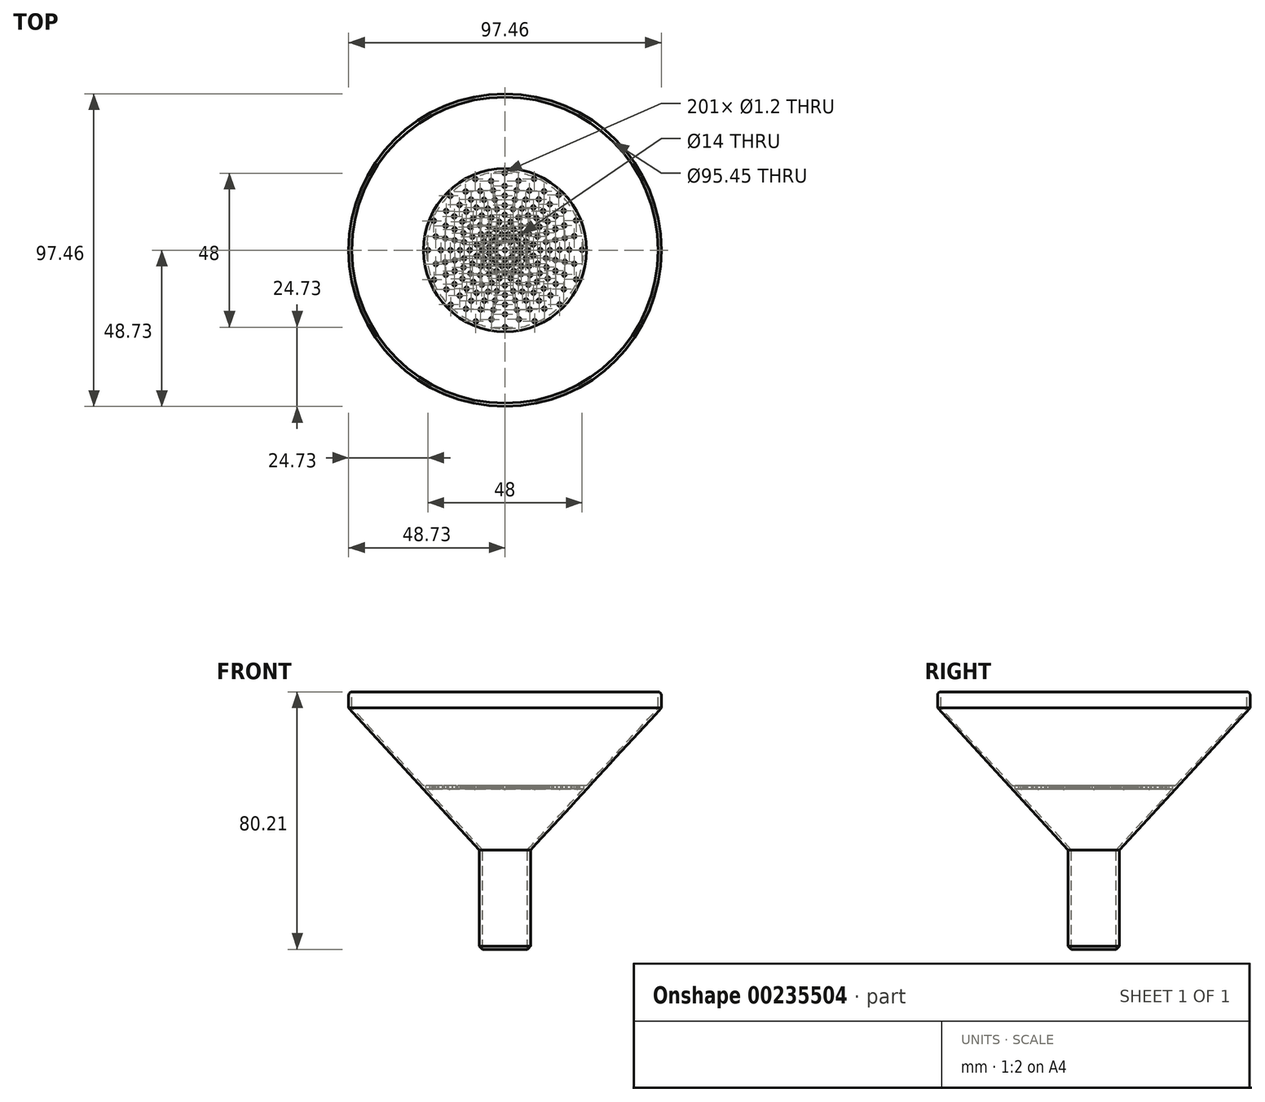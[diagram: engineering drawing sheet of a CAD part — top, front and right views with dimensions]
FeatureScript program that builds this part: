
annotation { "Feature Type Name" : "Feature", "Feature Type Description" : "" }
export const myFeature = defineFeature(function(context is Context, id is Id, definition is map)
    precondition{}
    {
        {
            var Q0;
            Q0=qCreatedBy(makeId("Front.planeOp"),FACE);
            var sketch = newSketch(context, id + "F0", { "sketchPlane" : qUnion([Q0])});
            skLineSegment(sketch, "E0", {"start": v(0, 0) * mm, "end": v(0, -31) * mm, "construction": true});
            skLineSegment(sketch, "E1", {"start": v(0, 0) * mm, "end": v(0, 43) * mm, "construction": true});
            skLineSegment(sketch, "E2", {"start": v(0, -31) * mm, "end": v(8, -31) * mm, "construction": true});
            skLineSegment(sketch, "E3", {"start": v(8, -31) * mm, "end": v(7, -31) * mm});
            skLineSegment(sketch, "E4", {"start": v(7, -31) * mm, "end": v(7, 0) * mm});
            skLineSegment(sketch, "E5", {"start": v(8, -31) * mm, "end": v(8, 0) * mm});
            skLineSegment(sketch, "E6", {"start": v(48.73, 44.2) * mm, "end": v(8, 0) * mm});
            skLineSegment(sketch, "E7", {"start": v(0, 43) * mm, "end": v(0, 41) * mm, "construction": true});
            skLineSegment(sketch, "E8", {"start": v(47.73, 44.2) * mm, "end": v(7, 0) * mm});
            skLineSegment(sketch, "E9", {"start": v(0, 0) * mm, "end": v(0, 20) * mm, "construction": true});
            skLineSegment(sketch, "E10", {"start": v(0, 20) * mm, "end": v(25.42, 20) * mm});
            skLineSegment(sketch, "E11", {"start": v(0, 20) * mm, "end": v(0, 19) * mm, "construction": true});
            skLineSegment(sketch, "E12", {"start": v(0, 19) * mm, "end": v(24.5, 19) * mm});
            skLineSegment(sketch, "E13", {"start": v(47.73, 44.2) * mm, "end": v(47.73, 44.2) * mm});
            skLineSegment(sketch, "E14", {"start": v(47.73, 44.2) * mm, "end": v(48.73, 44.2) * mm});
            skLineSegment(sketch, "E15", {"start": v(0, 19) * mm, "end": v(0, 20) * mm});
            skLineSegment(sketch, "E16", {"start": v(47.73, 44.2) * mm, "end": v(47.73, 49.2) * mm});
            skLineSegment(sketch, "E17", {"start": v(47.73, 49.2) * mm, "end": v(48.73, 49.2) * mm});
            skLineSegment(sketch, "E18", {"start": v(48.73, 49.2) * mm, "end": v(48.73, 44.2) * mm});
            skSolve(sketch);
        }
        {
            var Q0;
            Q0 = qSketchRegion(id + "F0", true);
            var Q1;
            Q1=sQuery(id+"F0.wireOp",EDGE,"E0");
            revolve(context, id + "F1", {"entities" : qUnion([Q0]), "axis" : qUnion([Q1]), "revolveType" : RevolveType.FULL});
        }
        {
            var Q0;
            Q0=makeQuery(id+"F1.opRevolve","SWEPT_EDGE",EDGE,{"disambiguationData":[OSD([sQuery(id+"F0.wireOp",EDGE,"E3"),sQuery(id+"F0.wireOp",EDGE,"E5")])]});
            chamfer(context, id + "F2", {"entities" : qUnion([Q0]), "width" : 1 * mm, "tangentPropagation" : true});
        }
        {
            var Q0;
            Q0=makeQuery(id+"F1.opRevolve","SWEPT_FACE",FACE,{"disambiguationData":[OSD([sQuery(id+"F0.wireOp",EDGE,"E10")])]});
            var sketch = newSketch(context, id + "F3", { "sketchPlane" : qUnion([Q0])});
            skCircle(sketch, "E19", {"center": v(0, 0) * mm, "radius": 0.5 * mm});
            skCircle(sketch, "E20", {"center": v(0, 0) * mm, "radius": 0.5 * mm, "construction": true});
            skCircle(sketch, "E21", {"center": v(0, 0) * mm, "radius": 24 * mm});
            skCircle(sketch, "E22", {"center": v(0, 0) * mm, "radius": 23 * mm});
            skCircle(sketch, "E23", {"center": v(0, 0) * mm, "radius": 22 * mm});
            skCircle(sketch, "E24", {"center": v(0, 0) * mm, "radius": 21 * mm});
            skCircle(sketch, "E25", {"center": v(0, 0) * mm, "radius": 20 * mm});
            skCircle(sketch, "E26", {"center": v(0, 0) * mm, "radius": 19 * mm});
            skCircle(sketch, "E27", {"center": v(0, 0) * mm, "radius": 18 * mm});
            skCircle(sketch, "E28", {"center": v(0, 0) * mm, "radius": 17 * mm});
            skCircle(sketch, "E29", {"center": v(0, 0) * mm, "radius": 16 * mm});
            skCircle(sketch, "E30", {"center": v(0, 0) * mm, "radius": 15 * mm});
            skCircle(sketch, "E31", {"center": v(0, 0) * mm, "radius": 14 * mm});
            skCircle(sketch, "E32", {"center": v(0, 0) * mm, "radius": 13 * mm});
            skCircle(sketch, "E33", {"center": v(0, 0) * mm, "radius": 12 * mm});
            skCircle(sketch, "E34", {"center": v(0, 0) * mm, "radius": 11 * mm});
            skCircle(sketch, "E35", {"center": v(0, 0) * mm, "radius": 10 * mm});
            skCircle(sketch, "E36", {"center": v(0, 0) * mm, "radius": 9 * mm});
            skCircle(sketch, "E37", {"center": v(0, 0) * mm, "radius": 8 * mm});
            skCircle(sketch, "E38", {"center": v(0, 0) * mm, "radius": 7 * mm});
            skCircle(sketch, "E39", {"center": v(0, 0) * mm, "radius": 6 * mm});
            skCircle(sketch, "E40", {"center": v(0, 0) * mm, "radius": 5 * mm});
            skCircle(sketch, "E41", {"center": v(0, 0) * mm, "radius": 4 * mm});
            skCircle(sketch, "E42", {"center": v(0, 0) * mm, "radius": 3 * mm});
            skCircle(sketch, "E43", {"center": v(0, 0) * mm, "radius": 2 * mm});
            skPoint(sketch, "E44", {"position": v(-2, 0) * mm});
            skPoint(sketch, "E45", {"position": v(-5, 0) * mm});
            skPoint(sketch, "E46", {"position": v(-6, 0) * mm});
            skPoint(sketch, "E47", {"position": v(-7, 0) * mm});
            skPoint(sketch, "E48", {"position": v(-8, 0) * mm});
            skPoint(sketch, "E49", {"position": v(-9, 0) * mm});
            skPoint(sketch, "E50", {"position": v(-10, 0) * mm});
            skPoint(sketch, "E51", {"position": v(-11, 0) * mm});
            skPoint(sketch, "E52", {"position": v(-12, 0) * mm});
            skPoint(sketch, "E53", {"position": v(-13, 0) * mm});
            skPoint(sketch, "E54", {"position": v(-14, 0) * mm});
            skPoint(sketch, "E55", {"position": v(-15, 0) * mm});
            skPoint(sketch, "E56", {"position": v(-16, 0) * mm});
            skPoint(sketch, "E57", {"position": v(-17, 0) * mm});
            skPoint(sketch, "E58", {"position": v(-18, 0) * mm});
            skPoint(sketch, "E59", {"position": v(-19, 0) * mm});
            skPoint(sketch, "E60", {"position": v(-20, 0) * mm});
            skPoint(sketch, "E61", {"position": v(-21, 0) * mm});
            skPoint(sketch, "E62", {"position": v(-22, 0) * mm});
            skPoint(sketch, "E63", {"position": v(-23, 0) * mm});
            skPoint(sketch, "E64", {"position": v(-24, 0) * mm});
            skPoint(sketch, "E65", {"position": v(4, 0) * mm});
            skPoint(sketch, "E66", {"position": v(5, 0) * mm});
            skPoint(sketch, "E67", {"position": v(6, 0) * mm});
            skPoint(sketch, "E68", {"position": v(7, 0) * mm});
            skPoint(sketch, "E69", {"position": v(8, 0) * mm});
            skPoint(sketch, "E70", {"position": v(9, 0) * mm});
            skPoint(sketch, "E71", {"position": v(10, 0) * mm});
            skPoint(sketch, "E72", {"position": v(11, 0) * mm});
            skPoint(sketch, "E73", {"position": v(12, 0) * mm});
            skPoint(sketch, "E74", {"position": v(13, 0) * mm});
            skPoint(sketch, "E75", {"position": v(14, 0) * mm});
            skPoint(sketch, "E76", {"position": v(15, 0) * mm});
            skPoint(sketch, "E77", {"position": v(16, 0.11) * mm});
            skPoint(sketch, "E78", {"position": v(17, 0.11) * mm});
            skPoint(sketch, "E79", {"position": v(18, 0.11) * mm});
            skPoint(sketch, "E80", {"position": v(19, 0.11) * mm});
            skPoint(sketch, "E81", {"position": v(20, 0.11) * mm});
            skPoint(sketch, "E82", {"position": v(21, 0.11) * mm});
            skPoint(sketch, "E83", {"position": v(22, 0.11) * mm});
            skPoint(sketch, "E84", {"position": v(23, 0.11) * mm});
            skPoint(sketch, "E85", {"position": v(24, 0.11) * mm});
            skLineSegment(sketch, "E86", {"start": v(24, 0.11) * mm, "end": v(-24, 0) * mm, "construction": true});
            skLineSegment(sketch, "E87", {"start": v(0, -24) * mm, "end": v(-0.11, 24) * mm});
            skLineSegment(sketch, "E88", {"start": v(0, 0) * mm, "end": v(-17.01, 16.93) * mm, "construction": true});
            skLineSegment(sketch, "E89", {"start": v(-24, 0) * mm, "end": v(24, 0.11) * mm, "construction": true});
            skLineSegment(sketch, "E90", {"start": v(-17.01, 16.93) * mm, "end": v(17.01, -16.93) * mm});
            skLineSegment(sketch, "E91", {"start": v(0, 0) * mm, "end": v(16.75, 17.19) * mm});
            skLineSegment(sketch, "E92", {"start": v(0, 0) * mm, "end": v(-16.93, -17.01) * mm});
            skLineSegment(sketch, "E93", {"start": v(0, 0) * mm, "end": v(9.1, 22.2) * mm, "construction": true});
            skLineSegment(sketch, "E94", {"start": v(9.1, 22.2) * mm, "end": v(-9.1, -22.2) * mm});
            skLineSegment(sketch, "E95", {"start": v(-24, 0) * mm, "end": v(24, 0.11) * mm});
            skLineSegment(sketch, "E96", {"start": v(0, 0) * mm, "end": v(22.15, 9.24) * mm});
            skLineSegment(sketch, "E97", {"start": v(22.15, 9.24) * mm, "end": v(-22.15, -9.24) * mm});
            skLineSegment(sketch, "E98", {"start": v(-22.2, 9.13) * mm, "end": v(0, 0) * mm});
            skLineSegment(sketch, "E99", {"start": v(0, 0) * mm, "end": v(22.2, -9.13) * mm});
            skLineSegment(sketch, "E100", {"start": v(0, 0) * mm, "end": v(-9.24, 22.15) * mm});
            skLineSegment(sketch, "E101", {"start": v(0, 0) * mm, "end": v(9.24, -22.15) * mm});
            skPoint(sketch, "E102", {"position": v(-3.7, -1.54) * mm});
            skPoint(sketch, "E103", {"position": v(-5.54, -2.3) * mm});
            skPoint(sketch, "E104", {"position": v(-6.46, -2.7) * mm});
            skPoint(sketch, "E105", {"position": v(-7.38, -3.08) * mm});
            skPoint(sketch, "E106", {"position": v(-8.3, -3.46) * mm});
            skPoint(sketch, "E107", {"position": v(-9.23, -3.85) * mm});
            skPoint(sketch, "E108", {"position": v(-10.15, -4.23) * mm});
            skPoint(sketch, "E109", {"position": v(-11.08, -4.62) * mm});
            skPoint(sketch, "E110", {"position": v(-12, -5) * mm});
            skPoint(sketch, "E111", {"position": v(-12.92, -5.39) * mm});
            skPoint(sketch, "E112", {"position": v(-13.84, -5.77) * mm});
            skPoint(sketch, "E113", {"position": v(-14.77, -6.16) * mm});
            skPoint(sketch, "E114", {"position": v(-15.7, -6.54) * mm});
            skPoint(sketch, "E115", {"position": v(-16.61, -6.93) * mm});
            skPoint(sketch, "E116", {"position": v(-17.54, -7.31) * mm});
            skPoint(sketch, "E117", {"position": v(-18.46, -7.7) * mm});
            skPoint(sketch, "E118", {"position": v(-19.38, -8.08) * mm});
            skPoint(sketch, "E119", {"position": v(-20.3, -8.47) * mm});
            skPoint(sketch, "E120", {"position": v(-21.23, -8.85) * mm});
            skPoint(sketch, "E121", {"position": v(-22.15, -9.24) * mm});
            skPoint(sketch, "E122", {"position": v(-1.41, -1.42) * mm});
            skPoint(sketch, "E123", {"position": v(-2.12, -2.13) * mm});
            skPoint(sketch, "E124", {"position": v(-2.82, -2.84) * mm});
            skPoint(sketch, "E125", {"position": v(-3.53, -3.54) * mm});
            skPoint(sketch, "E126", {"position": v(-4.23, -4.25) * mm});
            skPoint(sketch, "E127", {"position": v(-4.94, -4.96) * mm});
            skPoint(sketch, "E128", {"position": v(-5.64, -5.67) * mm});
            skPoint(sketch, "E129", {"position": v(-6.35, -6.38) * mm});
            skPoint(sketch, "E130", {"position": v(-7.05, -7.09) * mm});
            skPoint(sketch, "E131", {"position": v(-7.76, -7.8) * mm});
            skPoint(sketch, "E132", {"position": v(-8.47, -8.5) * mm});
            skPoint(sketch, "E133", {"position": v(-9.17, -9.21) * mm});
            skPoint(sketch, "E134", {"position": v(-9.88, -9.92) * mm});
            skPoint(sketch, "E135", {"position": v(-10.58, -10.63) * mm});
            skPoint(sketch, "E136", {"position": v(-11.29, -11.34) * mm});
            skPoint(sketch, "E137", {"position": v(-12, -12.05) * mm});
            skPoint(sketch, "E138", {"position": v(-12.7, -12.76) * mm});
            skPoint(sketch, "E139", {"position": v(-13.4, -13.47) * mm});
            skPoint(sketch, "E140", {"position": v(-14.1, -14.18) * mm});
            skPoint(sketch, "E141", {"position": v(-14.81, -14.88) * mm});
            skPoint(sketch, "E142", {"position": v(-15.52, -15.6) * mm});
            skPoint(sketch, "E143", {"position": v(-16.22, -16.3) * mm});
            skPoint(sketch, "E144", {"position": v(-16.93, -17.01) * mm});
            skPoint(sketch, "E145", {"position": v(-0.76, -1.85) * mm});
            skPoint(sketch, "E146", {"position": v(-1.14, -2.78) * mm});
            skPoint(sketch, "E147", {"position": v(-1.52, -3.7) * mm});
            skPoint(sketch, "E148", {"position": v(-1.9, -4.63) * mm});
            skPoint(sketch, "E149", {"position": v(-2.27, -5.55) * mm});
            skPoint(sketch, "E150", {"position": v(-2.65, -6.48) * mm});
            skPoint(sketch, "E151", {"position": v(-3.03, -7.4) * mm});
            skPoint(sketch, "E152", {"position": v(-3.41, -8.33) * mm});
            skPoint(sketch, "E153", {"position": v(-3.8, -9.25) * mm});
            skPoint(sketch, "E154", {"position": v(-4.17, -10.18) * mm});
            skPoint(sketch, "E155", {"position": v(-4.55, -11.1) * mm});
            skPoint(sketch, "E156", {"position": v(-4.94, -12.05) * mm});
            skPoint(sketch, "E157", {"position": v(-5.3, -12.96) * mm});
            skPoint(sketch, "E158", {"position": v(-5.69, -13.88) * mm});
            skPoint(sketch, "E159", {"position": v(-6.06, -14.8) * mm});
            skPoint(sketch, "E160", {"position": v(-6.44, -15.73) * mm});
            skPoint(sketch, "E161", {"position": v(-6.82, -16.66) * mm});
            skPoint(sketch, "E162", {"position": v(-7.2, -17.58) * mm});
            skPoint(sketch, "E163", {"position": v(-7.58, -18.5) * mm});
            skPoint(sketch, "E164", {"position": v(-7.96, -19.43) * mm});
            skPoint(sketch, "E165", {"position": v(-8.34, -20.36) * mm});
            skPoint(sketch, "E166", {"position": v(-8.72, -21.28) * mm});
            skPoint(sketch, "E167", {"position": v(-9.1, -22.2) * mm});
            skPoint(sketch, "E168", {"position": v(0, -24) * mm});
            skPoint(sketch, "E169", {"position": v(0, -23) * mm});
            skPoint(sketch, "E170", {"position": v(0, -22) * mm});
            skPoint(sketch, "E171", {"position": v(0, -20.91) * mm});
            skPoint(sketch, "E172", {"position": v(0, -20) * mm});
            skPoint(sketch, "E173", {"position": v(-0.01, -19) * mm});
            skPoint(sketch, "E174", {"position": v(0, -18) * mm});
            skPoint(sketch, "E175", {"position": v(0, -17) * mm});
            skPoint(sketch, "E176", {"position": v(-0.02, -16) * mm});
            skPoint(sketch, "E177", {"position": v(-0.02, -15) * mm});
            skPoint(sketch, "E178", {"position": v(-0.02, -14) * mm});
            skPoint(sketch, "E179", {"position": v(0, -13) * mm});
            skPoint(sketch, "E180", {"position": v(-0.03, -12) * mm});
            skPoint(sketch, "E181", {"position": v(-0.03, -11) * mm});
            skPoint(sketch, "E182", {"position": v(-0.03, -10) * mm});
            skPoint(sketch, "E183", {"position": v(-0.04, -9) * mm});
            skPoint(sketch, "E184", {"position": v(-0.04, -8) * mm});
            skPoint(sketch, "E185", {"position": v(-0.04, -7) * mm});
            skPoint(sketch, "E186", {"position": v(-0.08, -6) * mm});
            skPoint(sketch, "E187", {"position": v(-0.04, -5) * mm});
            skPoint(sketch, "E188", {"position": v(-0.04, -4) * mm});
            skPoint(sketch, "E189", {"position": v(-0.05, -2) * mm});
            skPoint(sketch, "E190", {"position": v(0.77, -1.85) * mm});
            skPoint(sketch, "E191", {"position": v(2.13, -2.12) * mm});
            skPoint(sketch, "E192", {"position": v(2.77, -1.14) * mm});
            skPoint(sketch, "E193", {"position": v(2.77, 1.15) * mm});
            skPoint(sketch, "E194", {"position": v(2.1, 2.15) * mm});
            skPoint(sketch, "E195", {"position": v(1.14, 2.78) * mm});
            skPoint(sketch, "E196", {"position": v(1.15, -2.77) * mm});
            skPoint(sketch, "E197", {"position": v(1.54, -3.7) * mm});
            skPoint(sketch, "E198", {"position": v(1.92, -4.61) * mm});
            skPoint(sketch, "E199", {"position": v(2.3, -5.54) * mm});
            skPoint(sketch, "E200", {"position": v(2.7, -6.46) * mm});
            skPoint(sketch, "E201", {"position": v(3.08, -7.38) * mm});
            skPoint(sketch, "E202", {"position": v(3.46, -8.3) * mm});
            skPoint(sketch, "E203", {"position": v(3.85, -9.23) * mm});
            skPoint(sketch, "E204", {"position": v(4.23, -10.15) * mm});
            skPoint(sketch, "E205", {"position": v(4.62, -11.08) * mm});
            skPoint(sketch, "E206", {"position": v(5, -12) * mm});
            skPoint(sketch, "E207", {"position": v(5.39, -12.92) * mm});
            skPoint(sketch, "E208", {"position": v(5.77, -13.84) * mm});
            skPoint(sketch, "E209", {"position": v(6.16, -14.77) * mm});
            skPoint(sketch, "E210", {"position": v(6.54, -15.7) * mm});
            skPoint(sketch, "E211", {"position": v(6.93, -16.61) * mm});
            skPoint(sketch, "E212", {"position": v(7.31, -17.54) * mm});
            skPoint(sketch, "E213", {"position": v(7.7, -18.46) * mm});
            skPoint(sketch, "E214", {"position": v(8.08, -19.38) * mm});
            skPoint(sketch, "E215", {"position": v(8.47, -20.3) * mm});
            skPoint(sketch, "E216", {"position": v(8.85, -21.23) * mm});
            skPoint(sketch, "E217", {"position": v(9.24, -22.15) * mm});
            skPoint(sketch, "E218", {"position": v(2.84, -2.82) * mm});
            skPoint(sketch, "E219", {"position": v(3.54, -3.53) * mm});
            skPoint(sketch, "E220", {"position": v(4.25, -4.23) * mm});
            skPoint(sketch, "E221", {"position": v(4.96, -4.94) * mm});
            skPoint(sketch, "E222", {"position": v(5.67, -5.64) * mm});
            skPoint(sketch, "E223", {"position": v(6.38, -6.35) * mm});
            skPoint(sketch, "E224", {"position": v(7.09, -7.05) * mm});
            skPoint(sketch, "E225", {"position": v(7.8, -7.76) * mm});
            skPoint(sketch, "E226", {"position": v(8.5, -8.47) * mm});
            skPoint(sketch, "E227", {"position": v(9.21, -9.17) * mm});
            skPoint(sketch, "E228", {"position": v(9.92, -9.88) * mm});
            skPoint(sketch, "E229", {"position": v(10.63, -10.58) * mm});
            skPoint(sketch, "E230", {"position": v(11.34, -11.29) * mm});
            skPoint(sketch, "E231", {"position": v(12.05, -12) * mm});
            skPoint(sketch, "E232", {"position": v(12.76, -12.7) * mm});
            skPoint(sketch, "E233", {"position": v(13.47, -13.4) * mm});
            skPoint(sketch, "E234", {"position": v(14.18, -14.1) * mm});
            skPoint(sketch, "E235", {"position": v(14.88, -14.81) * mm});
            skPoint(sketch, "E236", {"position": v(15.6, -15.52) * mm});
            skPoint(sketch, "E237", {"position": v(16.3, -16.22) * mm});
            skPoint(sketch, "E238", {"position": v(17.01, -16.93) * mm});
            skPoint(sketch, "E239", {"position": v(22.2, -9.13) * mm});
            skPoint(sketch, "E240", {"position": v(22.15, 9.24) * mm});
            skPoint(sketch, "E241", {"position": v(21.27, -8.75) * mm});
            skPoint(sketch, "E242", {"position": v(21.23, 8.85) * mm});
            skPoint(sketch, "E243", {"position": v(20.3, 8.47) * mm});
            skPoint(sketch, "E244", {"position": v(19.38, 8.08) * mm});
            skPoint(sketch, "E245", {"position": v(18.46, 7.7) * mm});
            skPoint(sketch, "E246", {"position": v(17.54, 7.31) * mm});
            skPoint(sketch, "E247", {"position": v(16.61, 6.93) * mm});
            skPoint(sketch, "E248", {"position": v(15.7, 6.54) * mm});
            skPoint(sketch, "E249", {"position": v(14.77, 6.16) * mm});
            skPoint(sketch, "E250", {"position": v(13.84, 5.77) * mm});
            skPoint(sketch, "E251", {"position": v(12.92, 5.39) * mm});
            skPoint(sketch, "E252", {"position": v(12, 5) * mm});
            skPoint(sketch, "E253", {"position": v(11.08, 4.62) * mm});
            skPoint(sketch, "E254", {"position": v(10.15, 4.23) * mm});
            skPoint(sketch, "E255", {"position": v(9.23, 3.85) * mm});
            skPoint(sketch, "E256", {"position": v(8.3, 3.46) * mm});
            skPoint(sketch, "E257", {"position": v(7.38, 3.08) * mm});
            skPoint(sketch, "E258", {"position": v(6.46, 2.7) * mm});
            skPoint(sketch, "E259", {"position": v(5.54, 2.3) * mm});
            skPoint(sketch, "E260", {"position": v(4.61, 1.92) * mm});
            skPoint(sketch, "E261", {"position": v(3.7, 1.54) * mm});
            skPoint(sketch, "E262", {"position": v(3.7, -1.52) * mm});
            skPoint(sketch, "E263", {"position": v(4.62, -1.9) * mm});
            skPoint(sketch, "E264", {"position": v(5.55, -2.28) * mm});
            skPoint(sketch, "E265", {"position": v(6.47, -2.66) * mm});
            skPoint(sketch, "E266", {"position": v(7.4, -3.04) * mm});
            skPoint(sketch, "E267", {"position": v(8.32, -3.42) * mm});
            skPoint(sketch, "E268", {"position": v(9.25, -3.8) * mm});
            skPoint(sketch, "E269", {"position": v(10.17, -4.19) * mm});
            skPoint(sketch, "E270", {"position": v(11.1, -4.57) * mm});
            skPoint(sketch, "E271", {"position": v(12.02, -4.95) * mm});
            skPoint(sketch, "E272", {"position": v(12.95, -5.33) * mm});
            skPoint(sketch, "E273", {"position": v(13.87, -5.7) * mm});
            skPoint(sketch, "E274", {"position": v(14.8, -6.09) * mm});
            skPoint(sketch, "E275", {"position": v(15.72, -6.47) * mm});
            skPoint(sketch, "E276", {"position": v(16.65, -6.85) * mm});
            skPoint(sketch, "E277", {"position": v(17.57, -7.23) * mm});
            skPoint(sketch, "E278", {"position": v(18.5, -7.6) * mm});
            skPoint(sketch, "E279", {"position": v(19.42, -8) * mm});
            skPoint(sketch, "E280", {"position": v(20.35, -8.37) * mm});
            skPoint(sketch, "E281", {"position": v(-2.77, 1.14) * mm});
            skPoint(sketch, "E282", {"position": v(-3.7, 1.52) * mm});
            skPoint(sketch, "E283", {"position": v(-4.62, 1.9) * mm});
            skPoint(sketch, "E284", {"position": v(-5.55, 2.28) * mm});
            skPoint(sketch, "E285", {"position": v(-6.47, 2.66) * mm});
            skPoint(sketch, "E286", {"position": v(-7.4, 3.04) * mm});
            skPoint(sketch, "E287", {"position": v(-8.32, 3.42) * mm});
            skPoint(sketch, "E288", {"position": v(-9.25, 3.8) * mm});
            skPoint(sketch, "E289", {"position": v(-10.17, 4.19) * mm});
            skPoint(sketch, "E290", {"position": v(-11.1, 4.57) * mm});
            skPoint(sketch, "E291", {"position": v(-12.02, 4.95) * mm});
            skPoint(sketch, "E292", {"position": v(-12.95, 5.33) * mm});
            skPoint(sketch, "E293", {"position": v(-13.87, 5.7) * mm});
            skPoint(sketch, "E294", {"position": v(-14.8, 6.09) * mm});
            skPoint(sketch, "E295", {"position": v(-15.72, 6.47) * mm});
            skPoint(sketch, "E296", {"position": v(-16.65, 6.85) * mm});
            skPoint(sketch, "E297", {"position": v(-17.57, 7.23) * mm});
            skPoint(sketch, "E298", {"position": v(-18.5, 7.6) * mm});
            skPoint(sketch, "E299", {"position": v(-19.42, 8) * mm});
            skPoint(sketch, "E300", {"position": v(-20.35, 8.37) * mm});
            skPoint(sketch, "E301", {"position": v(-21.27, 8.75) * mm});
            skPoint(sketch, "E302", {"position": v(-22.2, 9.13) * mm});
            skPoint(sketch, "E303", {"position": v(-1.42, 1.41) * mm});
            skPoint(sketch, "E304", {"position": v(-2.13, 2.12) * mm});
            skPoint(sketch, "E305", {"position": v(-2.84, 2.82) * mm});
            skPoint(sketch, "E306", {"position": v(-3.54, 3.53) * mm});
            skPoint(sketch, "E307", {"position": v(-4.25, 4.23) * mm});
            skPoint(sketch, "E308", {"position": v(-4.96, 4.94) * mm});
            skPoint(sketch, "E309", {"position": v(-5.67, 5.64) * mm});
            skPoint(sketch, "E310", {"position": v(-6.38, 6.35) * mm});
            skPoint(sketch, "E311", {"position": v(-7.09, 7.05) * mm});
            skPoint(sketch, "E312", {"position": v(-7.8, 7.76) * mm});
            skPoint(sketch, "E313", {"position": v(-8.5, 8.47) * mm});
            skPoint(sketch, "E314", {"position": v(-9.18, 9.13) * mm});
            skPoint(sketch, "E315", {"position": v(-9.92, 9.88) * mm});
            skPoint(sketch, "E316", {"position": v(-10.63, 10.58) * mm});
            skPoint(sketch, "E317", {"position": v(-11.34, 11.29) * mm});
            skPoint(sketch, "E318", {"position": v(-12.05, 12) * mm});
            skPoint(sketch, "E319", {"position": v(-12.76, 12.7) * mm});
            skPoint(sketch, "E320", {"position": v(-13.47, 13.4) * mm});
            skPoint(sketch, "E321", {"position": v(-14.18, 14.1) * mm});
            skPoint(sketch, "E322", {"position": v(-14.88, 14.81) * mm});
            skPoint(sketch, "E323", {"position": v(-15.6, 15.52) * mm});
            skPoint(sketch, "E324", {"position": v(-16.3, 16.22) * mm});
            skPoint(sketch, "E325", {"position": v(-17.01, 16.93) * mm});
            skPoint(sketch, "E326", {"position": v(-9.24, 22.15) * mm});
            skPoint(sketch, "E327", {"position": v(-0.11, 24) * mm});
            skPoint(sketch, "E328", {"position": v(9.1, 22.2) * mm});
            skPoint(sketch, "E329", {"position": v(16.75, 17.19) * mm});
            skPoint(sketch, "E330", {"position": v(-1.54, 3.7) * mm});
            skPoint(sketch, "E331", {"position": v(-2.3, 5.54) * mm});
            skPoint(sketch, "E332", {"position": v(-2.7, 6.46) * mm});
            skPoint(sketch, "E333", {"position": v(-3.08, 7.38) * mm});
            skPoint(sketch, "E334", {"position": v(-3.46, 8.3) * mm});
            skPoint(sketch, "E335", {"position": v(-3.85, 9.23) * mm});
            skPoint(sketch, "E336", {"position": v(-4.23, 10.15) * mm});
            skPoint(sketch, "E337", {"position": v(-4.62, 11.08) * mm});
            skPoint(sketch, "E338", {"position": v(-5, 12) * mm});
            skPoint(sketch, "E339", {"position": v(-5.39, 12.92) * mm});
            skPoint(sketch, "E340", {"position": v(-5.77, 13.84) * mm});
            skPoint(sketch, "E341", {"position": v(-6.16, 14.77) * mm});
            skPoint(sketch, "E342", {"position": v(-6.54, 15.7) * mm});
            skPoint(sketch, "E343", {"position": v(-6.93, 16.61) * mm});
            skPoint(sketch, "E344", {"position": v(-7.31, 17.54) * mm});
            skPoint(sketch, "E345", {"position": v(-8.08, 19.38) * mm});
            skPoint(sketch, "E346", {"position": v(-8.47, 20.3) * mm});
            skPoint(sketch, "E347", {"position": v(-0.07, 4) * mm});
            skPoint(sketch, "E348", {"position": v(-0.07, 6) * mm});
            skPoint(sketch, "E349", {"position": v(-0.07, 5) * mm});
            skPoint(sketch, "E350", {"position": v(-0.07, 7) * mm});
            skPoint(sketch, "E351", {"position": v(-0.08, 8) * mm});
            skPoint(sketch, "E352", {"position": v(-0.08, 9) * mm});
            skPoint(sketch, "E353", {"position": v(-0.11, 23) * mm});
            skPoint(sketch, "E354", {"position": v(-0.1, 22) * mm});
            skPoint(sketch, "E355", {"position": v(-0.1, 21) * mm});
            skPoint(sketch, "E356", {"position": v(-0.1, 20) * mm});
            skPoint(sketch, "E357", {"position": v(-0.1, 19) * mm});
            skPoint(sketch, "E358", {"position": v(-0.1, 18) * mm});
            skPoint(sketch, "E359", {"position": v(-0.1, 17) * mm});
            skPoint(sketch, "E360", {"position": v(-0.1, 16) * mm});
            skPoint(sketch, "E361", {"position": v(-0.1, 15) * mm});
            skPoint(sketch, "E362", {"position": v(-0.09, 14) * mm});
            skPoint(sketch, "E363", {"position": v(-0.09, 13) * mm});
            skPoint(sketch, "E364", {"position": v(-0.09, 12) * mm});
            skPoint(sketch, "E365", {"position": v(-0.08, 11) * mm});
            skPoint(sketch, "E366", {"position": v(-0.08, 10) * mm});
            skPoint(sketch, "E367", {"position": v(8.72, 21.28) * mm});
            skPoint(sketch, "E368", {"position": v(8.34, 20.36) * mm});
            skPoint(sketch, "E369", {"position": v(7.96, 19.43) * mm});
            skPoint(sketch, "E370", {"position": v(7.58, 18.5) * mm});
            skPoint(sketch, "E371", {"position": v(7.2, 17.58) * mm});
            skPoint(sketch, "E372", {"position": v(6.82, 16.66) * mm});
            skPoint(sketch, "E373", {"position": v(6.44, 15.73) * mm});
            skPoint(sketch, "E374", {"position": v(6.06, 14.8) * mm});
            skPoint(sketch, "E375", {"position": v(5.69, 13.88) * mm});
            skPoint(sketch, "E376", {"position": v(5.3, 12.96) * mm});
            skPoint(sketch, "E377", {"position": v(4.93, 12.03) * mm});
            skPoint(sketch, "E378", {"position": v(4.55, 11.1) * mm});
            skPoint(sketch, "E379", {"position": v(4.17, 10.18) * mm});
            skPoint(sketch, "E380", {"position": v(3.8, 9.25) * mm});
            skPoint(sketch, "E381", {"position": v(3.41, 8.33) * mm});
            skPoint(sketch, "E382", {"position": v(3.03, 7.4) * mm});
            skPoint(sketch, "E383", {"position": v(2.65, 6.48) * mm});
            skPoint(sketch, "E384", {"position": v(2.27, 5.55) * mm});
            skPoint(sketch, "E385", {"position": v(1.9, 4.63) * mm});
            skPoint(sketch, "E386", {"position": v(1.52, 3.7) * mm});
            skPoint(sketch, "E387", {"position": v(2.8, 2.86) * mm});
            skPoint(sketch, "E388", {"position": v(3.5, 3.58) * mm});
            skPoint(sketch, "E389", {"position": v(4.19, 4.3) * mm});
            skPoint(sketch, "E390", {"position": v(4.89, 5.01) * mm});
            skPoint(sketch, "E391", {"position": v(5.58, 5.73) * mm});
            skPoint(sketch, "E392", {"position": v(6.28, 6.44) * mm});
            skPoint(sketch, "E393", {"position": v(6.98, 7.16) * mm});
            skPoint(sketch, "E394", {"position": v(7.68, 7.88) * mm});
            skPoint(sketch, "E395", {"position": v(8.38, 8.6) * mm});
            skPoint(sketch, "E396", {"position": v(9.07, 9.3) * mm});
            skPoint(sketch, "E397", {"position": v(9.77, 10.02) * mm});
            skPoint(sketch, "E398", {"position": v(10.47, 10.74) * mm});
            skPoint(sketch, "E399", {"position": v(11.17, 11.46) * mm});
            skPoint(sketch, "E400", {"position": v(11.87, 12.17) * mm});
            skPoint(sketch, "E401", {"position": v(12.56, 12.89) * mm});
            skPoint(sketch, "E402", {"position": v(13.26, 13.6) * mm});
            skPoint(sketch, "E403", {"position": v(13.96, 14.32) * mm});
            skPoint(sketch, "E404", {"position": v(14.66, 15.04) * mm});
            skPoint(sketch, "E405", {"position": v(15.36, 15.75) * mm});
            skPoint(sketch, "E406", {"position": v(16.05, 16.47) * mm});
            skPoint(sketch, "E407", {"position": v(-1.92, 4.61) * mm});
            skLineSegment(sketch, "E408", {"start": v(0, 0) * mm, "end": v(-4.74, 23.53) * mm, "construction": true});
            skPoint(sketch, "E409", {"position": v(-4.74, 23.53) * mm});
            skPoint(sketch, "E410", {"position": v(-4.54, 22.55) * mm});
            skPoint(sketch, "E411", {"position": v(-4.34, 21.57) * mm});
            skPoint(sketch, "E412", {"position": v(-4.15, 20.59) * mm});
            skPoint(sketch, "E413", {"position": v(-3.94, 19.56) * mm});
            skPoint(sketch, "E414", {"position": v(-3.75, 18.63) * mm});
            skPoint(sketch, "E415", {"position": v(-3.55, 17.65) * mm});
            skPoint(sketch, "E416", {"position": v(-3.36, 16.67) * mm});
            skPoint(sketch, "E417", {"position": v(-3.16, 15.69) * mm});
            skPoint(sketch, "E418", {"position": v(-2.96, 14.7) * mm});
            skPoint(sketch, "E419", {"position": v(-2.76, 13.72) * mm});
            skPoint(sketch, "E420", {"position": v(-2.57, 12.74) * mm});
            skPoint(sketch, "E421", {"position": v(-2.37, 11.76) * mm});
            skPoint(sketch, "E422", {"position": v(-2.17, 10.78) * mm});
            skPoint(sketch, "E423", {"position": v(-1.97, 9.8) * mm});
            skPoint(sketch, "E424", {"position": v(-1.78, 8.82) * mm});
            skPoint(sketch, "E425", {"position": v(-1.58, 7.84) * mm});
            skPoint(sketch, "E426", {"position": v(-1.38, 6.86) * mm});
            skPoint(sketch, "E427", {"position": v(-1.18, 5.88) * mm});
            skPoint(sketch, "E428", {"position": v(-0.99, 4.9) * mm});
            skPoint(sketch, "E429", {"position": v(-0.79, 3.92) * mm});
            skLineSegment(sketch, "E430", {"start": v(0, 0) * mm, "end": v(4.59, 23.56) * mm, "construction": true});
            skPoint(sketch, "E431", {"position": v(4.59, 23.56) * mm});
            skPoint(sketch, "E432", {"position": v(4.4, 22.58) * mm});
            skPoint(sketch, "E433", {"position": v(4.2, 21.6) * mm});
            skPoint(sketch, "E434", {"position": v(4.02, 20.61) * mm});
            skPoint(sketch, "E435", {"position": v(3.82, 19.63) * mm});
            skPoint(sketch, "E436", {"position": v(3.63, 18.65) * mm});
            skPoint(sketch, "E437", {"position": v(3.44, 17.67) * mm});
            skPoint(sketch, "E438", {"position": v(3.25, 16.69) * mm});
            skPoint(sketch, "E439", {"position": v(3.06, 15.7) * mm});
            skPoint(sketch, "E440", {"position": v(2.87, 14.72) * mm});
            skPoint(sketch, "E441", {"position": v(2.68, 13.74) * mm});
            skPoint(sketch, "E442", {"position": v(2.49, 12.76) * mm});
            skPoint(sketch, "E443", {"position": v(2.3, 11.78) * mm});
            skPoint(sketch, "E444", {"position": v(2.1, 10.8) * mm});
            skPoint(sketch, "E445", {"position": v(1.91, 9.82) * mm});
            skPoint(sketch, "E446", {"position": v(1.72, 8.83) * mm});
            skPoint(sketch, "E447", {"position": v(1.53, 7.85) * mm});
            skPoint(sketch, "E448", {"position": v(1.34, 6.87) * mm});
            skPoint(sketch, "E449", {"position": v(1.15, 5.89) * mm});
            skPoint(sketch, "E450", {"position": v(0.96, 4.9) * mm});
            skPoint(sketch, "E451", {"position": v(0.76, 3.93) * mm});
            skLineSegment(sketch, "E452", {"start": v(0, 0) * mm, "end": v(13.29, 19.99) * mm, "construction": true});
            skLineSegment(sketch, "E453", {"start": v(0, 0) * mm, "end": v(19.92, 13.38) * mm, "construction": true});
            skPoint(sketch, "E454", {"position": v(13.29, 19.99) * mm});
            skPoint(sketch, "E455", {"position": v(19.92, 13.38) * mm});
            skPoint(sketch, "E456", {"position": v(12.73, 19.15) * mm});
            skPoint(sketch, "E457", {"position": v(19.1, 12.82) * mm});
            skPoint(sketch, "E458", {"position": v(12.18, 18.32) * mm});
            skPoint(sketch, "E459", {"position": v(11.63, 17.49) * mm});
            skPoint(sketch, "E460", {"position": v(11.07, 16.66) * mm});
            skPoint(sketch, "E461", {"position": v(10.52, 15.82) * mm});
            skPoint(sketch, "E462", {"position": v(9.96, 15) * mm});
            skPoint(sketch, "E463", {"position": v(9.41, 14.16) * mm});
            skPoint(sketch, "E464", {"position": v(8.86, 13.32) * mm});
            skPoint(sketch, "E465", {"position": v(8.3, 12.5) * mm});
            skPoint(sketch, "E466", {"position": v(7.75, 11.66) * mm});
            skPoint(sketch, "E467", {"position": v(7.2, 10.83) * mm});
            skPoint(sketch, "E468", {"position": v(6.64, 10) * mm});
            skPoint(sketch, "E469", {"position": v(6.09, 9.16) * mm});
            skPoint(sketch, "E470", {"position": v(5.54, 8.33) * mm});
            skPoint(sketch, "E471", {"position": v(4.98, 7.5) * mm});
            skPoint(sketch, "E472", {"position": v(4.43, 6.66) * mm});
            skPoint(sketch, "E473", {"position": v(3.88, 5.83) * mm});
            skPoint(sketch, "E474", {"position": v(3.32, 5) * mm});
            skPoint(sketch, "E475", {"position": v(2.77, 4.16) * mm});
            skPoint(sketch, "E476", {"position": v(2.21, 3.33) * mm});
            skPoint(sketch, "E477", {"position": v(1.66, 2.5) * mm});
            skPoint(sketch, "E478", {"position": v(18.26, 12.27) * mm});
            skPoint(sketch, "E479", {"position": v(17.43, 11.7) * mm});
            skPoint(sketch, "E480", {"position": v(16.6, 11.15) * mm});
            skPoint(sketch, "E481", {"position": v(15.77, 10.6) * mm});
            skPoint(sketch, "E482", {"position": v(14.94, 10.04) * mm});
            skPoint(sketch, "E483", {"position": v(14.11, 9.48) * mm});
            skPoint(sketch, "E484", {"position": v(13.28, 8.92) * mm});
            skPoint(sketch, "E485", {"position": v(12.45, 8.36) * mm});
            skPoint(sketch, "E486", {"position": v(11.62, 7.8) * mm});
            skPoint(sketch, "E487", {"position": v(10.8, 7.25) * mm});
            skPoint(sketch, "E488", {"position": v(9.96, 6.7) * mm});
            skPoint(sketch, "E489", {"position": v(9.13, 6.13) * mm});
            skPoint(sketch, "E490", {"position": v(8.3, 5.58) * mm});
            skPoint(sketch, "E491", {"position": v(7.47, 5.02) * mm});
            skPoint(sketch, "E492", {"position": v(6.64, 4.46) * mm});
            skPoint(sketch, "E493", {"position": v(5.81, 3.9) * mm});
            skPoint(sketch, "E494", {"position": v(4.98, 3.35) * mm});
            skPoint(sketch, "E495", {"position": v(4.15, 2.79) * mm});
            skPoint(sketch, "E496", {"position": v(3.32, 2.23) * mm});
            skPoint(sketch, "E497", {"position": v(2.5, 1.67) * mm});
            skLineSegment(sketch, "E498", {"start": v(0, 0) * mm, "end": v(23.53, 4.74) * mm, "construction": true});
            skPoint(sketch, "E499", {"position": v(2.94, 0.6) * mm});
            skPoint(sketch, "E500", {"position": v(3.92, 0.79) * mm});
            skPoint(sketch, "E501", {"position": v(4.9, 0.99) * mm});
            skPoint(sketch, "E502", {"position": v(5.88, 1.18) * mm});
            skPoint(sketch, "E503", {"position": v(6.86, 1.38) * mm});
            skPoint(sketch, "E504", {"position": v(7.84, 1.58) * mm});
            skPoint(sketch, "E505", {"position": v(8.82, 1.78) * mm});
            skPoint(sketch, "E506", {"position": v(9.8, 1.97) * mm});
            skPoint(sketch, "E507", {"position": v(10.78, 2.17) * mm});
            skPoint(sketch, "E508", {"position": v(11.76, 2.37) * mm});
            skPoint(sketch, "E509", {"position": v(12.74, 2.57) * mm});
            skPoint(sketch, "E510", {"position": v(13.72, 2.76) * mm});
            skPoint(sketch, "E511", {"position": v(14.7, 2.96) * mm});
            skPoint(sketch, "E512", {"position": v(15.69, 3.16) * mm});
            skPoint(sketch, "E513", {"position": v(16.67, 3.36) * mm});
            skPoint(sketch, "E514", {"position": v(17.65, 3.55) * mm});
            skPoint(sketch, "E515", {"position": v(18.63, 3.75) * mm});
            skPoint(sketch, "E516", {"position": v(19.6, 3.95) * mm});
            skPoint(sketch, "E517", {"position": v(20.59, 4.15) * mm});
            skPoint(sketch, "E518", {"position": v(21.57, 4.34) * mm});
            skPoint(sketch, "E519", {"position": v(22.55, 4.54) * mm});
            skPoint(sketch, "E520", {"position": v(23.53, 4.74) * mm});
            skLineSegment(sketch, "E521", {"start": v(0, 0) * mm, "end": v(23.55, -4.63) * mm, "construction": true});
            skPoint(sketch, "E522", {"position": v(2.94, -0.58) * mm});
            skPoint(sketch, "E523", {"position": v(3.92, -0.77) * mm});
            skPoint(sketch, "E524", {"position": v(4.9, -0.96) * mm});
            skPoint(sketch, "E525", {"position": v(5.89, -1.16) * mm});
            skPoint(sketch, "E526", {"position": v(6.87, -1.35) * mm});
            skPoint(sketch, "E527", {"position": v(7.85, -1.54) * mm});
            skPoint(sketch, "E528", {"position": v(8.83, -1.73) * mm});
            skPoint(sketch, "E529", {"position": v(9.81, -1.93) * mm});
            skPoint(sketch, "E530", {"position": v(10.8, -2.12) * mm});
            skPoint(sketch, "E531", {"position": v(11.77, -2.31) * mm});
            skPoint(sketch, "E532", {"position": v(12.76, -2.5) * mm});
            skPoint(sketch, "E533", {"position": v(13.74, -2.7) * mm});
            skPoint(sketch, "E534", {"position": v(14.72, -2.9) * mm});
            skPoint(sketch, "E535", {"position": v(15.7, -3.08) * mm});
            skPoint(sketch, "E536", {"position": v(16.68, -3.28) * mm});
            skPoint(sketch, "E537", {"position": v(17.66, -3.47) * mm});
            skPoint(sketch, "E538", {"position": v(18.64, -3.66) * mm});
            skPoint(sketch, "E539", {"position": v(19.62, -3.86) * mm});
            skPoint(sketch, "E540", {"position": v(20.6, -4.05) * mm});
            skPoint(sketch, "E541", {"position": v(21.59, -4.24) * mm});
            skPoint(sketch, "E542", {"position": v(22.57, -4.43) * mm});
            skPoint(sketch, "E543", {"position": v(23.55, -4.63) * mm});
            skLineSegment(sketch, "E544", {"start": v(0, 0) * mm, "end": v(19.99, -13.29) * mm, "construction": true});
            skPoint(sketch, "E545", {"position": v(2.5, -1.66) * mm});
            skPoint(sketch, "E546", {"position": v(3.33, -2.21) * mm});
            skPoint(sketch, "E547", {"position": v(4.16, -2.77) * mm});
            skPoint(sketch, "E548", {"position": v(5, -3.32) * mm});
            skPoint(sketch, "E549", {"position": v(5.83, -3.88) * mm});
            skPoint(sketch, "E550", {"position": v(6.66, -4.43) * mm});
            skPoint(sketch, "E551", {"position": v(7.5, -4.98) * mm});
            skLineSegment(sketch, "E552", {"start": v(0, 0) * mm, "end": v(4.74, -23.53) * mm, "construction": true});
            skLineSegment(sketch, "E553", {"start": v(0, 0) * mm, "end": v(13.38, -19.92) * mm, "construction": true});
            skLineSegment(sketch, "E554", {"start": v(0, 0) * mm, "end": v(-4.63, -23.55) * mm, "construction": true});
            skLineSegment(sketch, "E555", {"start": v(0, 0) * mm, "end": v(-13.29, -19.99) * mm, "construction": true});
            skLineSegment(sketch, "E556", {"start": v(0, 0) * mm, "end": v(-19.92, -13.38) * mm, "construction": true});
            skLineSegment(sketch, "E557", {"start": v(0, 0) * mm, "end": v(-23.53, -4.74) * mm, "construction": true});
            skLineSegment(sketch, "E558", {"start": v(0, 0) * mm, "end": v(-23.55, 4.63) * mm, "construction": true});
            skLineSegment(sketch, "E559", {"start": v(0, 0) * mm, "end": v(-19.99, 13.29) * mm, "construction": true});
            skLineSegment(sketch, "E560", {"start": v(0, 0) * mm, "end": v(-13.38, 19.92) * mm, "construction": true});
            skPoint(sketch, "E561", {"position": v(-13.38, 19.92) * mm});
            skPoint(sketch, "E562", {"position": v(-19.99, 13.29) * mm});
            skPoint(sketch, "E563", {"position": v(-23.55, 4.63) * mm});
            skPoint(sketch, "E564", {"position": v(-23.53, -4.74) * mm});
            skPoint(sketch, "E565", {"position": v(-19.92, -13.38) * mm});
            skPoint(sketch, "E566", {"position": v(-13.29, -19.99) * mm});
            skPoint(sketch, "E567", {"position": v(-4.63, -23.55) * mm});
            skPoint(sketch, "E568", {"position": v(4.74, -23.53) * mm});
            skPoint(sketch, "E569", {"position": v(13.38, -19.92) * mm});
            skPoint(sketch, "E570", {"position": v(19.99, -13.29) * mm});
            skPoint(sketch, "E571", {"position": v(19.15, -12.73) * mm});
            skPoint(sketch, "E572", {"position": v(18.32, -12.18) * mm});
            skPoint(sketch, "E573", {"position": v(17.49, -11.63) * mm});
            skPoint(sketch, "E574", {"position": v(16.66, -11.07) * mm});
            skPoint(sketch, "E575", {"position": v(15.82, -10.52) * mm});
            skPoint(sketch, "E576", {"position": v(15, -9.96) * mm});
            skPoint(sketch, "E577", {"position": v(14.16, -9.41) * mm});
            skPoint(sketch, "E578", {"position": v(13.32, -8.86) * mm});
            skPoint(sketch, "E579", {"position": v(12.5, -8.3) * mm});
            skPoint(sketch, "E580", {"position": v(11.66, -7.75) * mm});
            skPoint(sketch, "E581", {"position": v(10.83, -7.2) * mm});
            skPoint(sketch, "E582", {"position": v(10, -6.64) * mm});
            skPoint(sketch, "E583", {"position": v(9.16, -6.09) * mm});
            skPoint(sketch, "E584", {"position": v(8.33, -5.54) * mm});
            skPoint(sketch, "E585", {"position": v(1.12, -1.66) * mm});
            skPoint(sketch, "E586", {"position": v(1.67, -1.1) * mm});
            skPoint(sketch, "E587", {"position": v(1.85, -0.76) * mm});
            skPoint(sketch, "E588", {"position": v(1.96, -0.39) * mm});
            skPoint(sketch, "E589", {"position": v(1.96, 0.4) * mm});
            skPoint(sketch, "E590", {"position": v(1.85, 0.77) * mm});
            skPoint(sketch, "E591", {"position": v(1.66, 1.12) * mm});
            skPoint(sketch, "E592", {"position": v(0.4, -1.96) * mm});
            skPoint(sketch, "E593", {"position": v(-0.39, -1.96) * mm});
            skPoint(sketch, "E594", {"position": v(-1.1, -1.67) * mm});
            skPoint(sketch, "E595", {"position": v(-1.66, -1.12) * mm});
            skPoint(sketch, "E596", {"position": v(-1.85, -0.77) * mm});
            skPoint(sketch, "E597", {"position": v(-1.96, -0.4) * mm});
            skPoint(sketch, "E598", {"position": v(-1.96, 0.39) * mm});
            skPoint(sketch, "E599", {"position": v(-1.85, 0.77) * mm});
            skPoint(sketch, "E600", {"position": v(-1.67, 1.1) * mm});
            skPoint(sketch, "E601", {"position": v(-1.12, 1.66) * mm});
            skPoint(sketch, "E602", {"position": v(-0.77, 1.85) * mm});
            skPoint(sketch, "E603", {"position": v(-0.4, 1.96) * mm});
            skPoint(sketch, "E604", {"position": v(-0.06, 2) * mm});
            skPoint(sketch, "E605", {"position": v(0.38, 1.96) * mm});
            skPoint(sketch, "E606", {"position": v(0.76, 1.85) * mm});
            skPoint(sketch, "E607", {"position": v(1.1, 1.67) * mm});
            skPoint(sketch, "E608", {"position": v(1.4, 1.43) * mm});
            skPoint(sketch, "E609", {"position": v(2, 0.06) * mm});
            skPoint(sketch, "E610", {"position": v(3, 0.06) * mm});
            skPoint(sketch, "E611", {"position": v(1.67, -2.5) * mm});
            skPoint(sketch, "E612", {"position": v(0.6, -2.94) * mm});
            skPoint(sketch, "E613", {"position": v(-0.05, -3) * mm});
            skPoint(sketch, "E614", {"position": v(-0.58, -2.94) * mm});
            skPoint(sketch, "E615", {"position": v(-2.5, -1.67) * mm});
            skPoint(sketch, "E616", {"position": v(-2.77, -1.15) * mm});
            skPoint(sketch, "E617", {"position": v(-2.94, -0.6) * mm});
            skPoint(sketch, "E618", {"position": v(-3.32, -2.23) * mm});
            skPoint(sketch, "E619", {"position": v(-3.92, -0.79) * mm});
            skPoint(sketch, "E620", {"position": v(-4, 0.05) * mm});
            skPoint(sketch, "E621", {"position": v(-3.92, 0.77) * mm});
            skPoint(sketch, "E622", {"position": v(-3, 0.05) * mm});
            skPoint(sketch, "E623", {"position": v(-2.94, 0.58) * mm});
            skPoint(sketch, "E624", {"position": v(-0.6, 2.94) * mm});
            skPoint(sketch, "E625", {"position": v(0.57, 2.94) * mm});
            skPoint(sketch, "E626", {"position": v(-1.67, 2.5) * mm});
            skPoint(sketch, "E627", {"position": v(-1.15, 2.77) * mm});
            skPoint(sketch, "E628", {"position": v(-0.06, 3) * mm});
            skPoint(sketch, "E629", {"position": v(-2.23, 3.32) * mm});
            skPoint(sketch, "E630", {"position": v(-3.33, 2.21) * mm});
            skPoint(sketch, "E631", {"position": v(-0.1, 0.5) * mm});
            skPoint(sketch, "E632", {"position": v(-0.5, 0.06) * mm});
            skPoint(sketch, "E633", {"position": v(0.5, 0.06) * mm});
            skPoint(sketch, "E634", {"position": v(-0.06, -0.5) * mm});
            skPoint(sketch, "E635", {"position": v(-0.42, -0.28) * mm});
            skPoint(sketch, "E636", {"position": v(0.35, -0.35) * mm});
            skPoint(sketch, "E637", {"position": v(-0.35, 0.35) * mm});
            skPoint(sketch, "E638", {"position": v(0.28, 0.42) * mm});
            skPoint(sketch, "E639", {"position": v(0.2, -0.46) * mm});
            skPoint(sketch, "E640", {"position": v(-4.15, -2.79) * mm});
            skPoint(sketch, "E641", {"position": v(-4.61, -1.92) * mm});
            skPoint(sketch, "E642", {"position": v(-4.9, -0.99) * mm});
            skPoint(sketch, "E643", {"position": v(-4.9, 0.96) * mm});
            skPoint(sketch, "E644", {"position": v(-4.16, 2.77) * mm});
            skPoint(sketch, "E645", {"position": v(-2.79, 4.15) * mm});
            skPoint(sketch, "E646", {"position": v(-3.35, 4.98) * mm});
            skPoint(sketch, "E647", {"position": v(-5, 3.32) * mm});
            skPoint(sketch, "E648", {"position": v(-5.89, 1.16) * mm});
            skPoint(sketch, "E649", {"position": v(-5.88, -1.18) * mm});
            skPoint(sketch, "E650", {"position": v(-4.98, -3.35) * mm});
            skPoint(sketch, "E651", {"position": v(-3.32, -5) * mm});
            skPoint(sketch, "E652", {"position": v(-1.16, -5.89) * mm});
            skPoint(sketch, "E653", {"position": v(-0.77, -3.92) * mm});
            skPoint(sketch, "E654", {"position": v(-0.96, -4.9) * mm});
            skPoint(sketch, "E655", {"position": v(0.79, -3.92) * mm});
            skPoint(sketch, "E656", {"position": v(0.99, -4.9) * mm});
            skPoint(sketch, "E657", {"position": v(1.16, -5.89) * mm});
            skPoint(sketch, "E658", {"position": v(1.38, -6.86) * mm});
            skPoint(sketch, "E659", {"position": v(2.23, -3.32) * mm});
            skPoint(sketch, "E660", {"position": v(2.79, -4.15) * mm});
            skPoint(sketch, "E661", {"position": v(3.35, -4.98) * mm});
            skPoint(sketch, "E662", {"position": v(3.9, -5.81) * mm});
            skPoint(sketch, "E663", {"position": v(-3.9, 5.81) * mm});
            skPoint(sketch, "E664", {"position": v(-5.83, 3.88) * mm});
            skPoint(sketch, "E665", {"position": v(-6.87, 1.35) * mm});
            skPoint(sketch, "E666", {"position": v(-6.86, -1.38) * mm});
            skPoint(sketch, "E667", {"position": v(-5.81, -3.9) * mm});
            skPoint(sketch, "E668", {"position": v(-3.88, -5.83) * mm});
            skPoint(sketch, "E669", {"position": v(-1.35, -6.87) * mm});
            skPoint(sketch, "E670", {"position": v(-4.46, 6.64) * mm});
            skPoint(sketch, "E671", {"position": v(4.46, -6.64) * mm});
            skPoint(sketch, "E672", {"position": v(1.58, -7.84) * mm});
            skPoint(sketch, "E673", {"position": v(-1.54, -7.85) * mm});
            skPoint(sketch, "E674", {"position": v(-4.43, -6.66) * mm});
            skPoint(sketch, "E675", {"position": v(-6.64, -4.46) * mm});
            skPoint(sketch, "E676", {"position": v(-7.84, -1.58) * mm});
            skPoint(sketch, "E677", {"position": v(-7.85, 1.54) * mm});
            skPoint(sketch, "E678", {"position": v(-6.66, 4.43) * mm});
            skPoint(sketch, "E679", {"position": v(5.02, -7.47) * mm});
            skPoint(sketch, "E680", {"position": v(5.58, -8.3) * mm});
            skPoint(sketch, "E681", {"position": v(6.13, -9.13) * mm});
            skPoint(sketch, "E682", {"position": v(6.7, -9.96) * mm});
            skPoint(sketch, "E683", {"position": v(7.25, -10.8) * mm});
            skPoint(sketch, "E684", {"position": v(7.8, -11.62) * mm});
            skPoint(sketch, "E685", {"position": v(8.36, -12.45) * mm});
            skPoint(sketch, "E686", {"position": v(8.92, -13.28) * mm});
            skPoint(sketch, "E687", {"position": v(9.48, -14.11) * mm});
            skPoint(sketch, "E688", {"position": v(10.04, -14.94) * mm});
            skPoint(sketch, "E689", {"position": v(10.6, -15.77) * mm});
            skPoint(sketch, "E690", {"position": v(11.15, -16.6) * mm});
            skPoint(sketch, "E691", {"position": v(11.7, -17.43) * mm});
            skPoint(sketch, "E692", {"position": v(12.27, -18.26) * mm});
            skPoint(sketch, "E693", {"position": v(12.82, -19.1) * mm});
            skPoint(sketch, "E694", {"position": v(4.54, -22.55) * mm});
            skPoint(sketch, "E695", {"position": v(4.34, -21.57) * mm});
            skPoint(sketch, "E696", {"position": v(4.15, -20.59) * mm});
            skPoint(sketch, "E697", {"position": v(3.95, -19.6) * mm});
            skPoint(sketch, "E698", {"position": v(3.75, -18.63) * mm});
            skPoint(sketch, "E699", {"position": v(3.55, -17.65) * mm});
            skPoint(sketch, "E700", {"position": v(3.36, -16.67) * mm});
            skPoint(sketch, "E701", {"position": v(3.16, -15.69) * mm});
            skPoint(sketch, "E702", {"position": v(2.96, -14.7) * mm});
            skPoint(sketch, "E703", {"position": v(2.76, -13.72) * mm});
            skPoint(sketch, "E704", {"position": v(2.57, -12.74) * mm});
            skPoint(sketch, "E705", {"position": v(2.37, -11.76) * mm});
            skPoint(sketch, "E706", {"position": v(2.17, -10.78) * mm});
            skPoint(sketch, "E707", {"position": v(1.97, -9.8) * mm});
            skPoint(sketch, "E708", {"position": v(1.78, -8.82) * mm});
            skPoint(sketch, "E709", {"position": v(-1.73, -8.83) * mm});
            skPoint(sketch, "E710", {"position": v(-1.93, -9.81) * mm});
            skPoint(sketch, "E711", {"position": v(-2.12, -10.8) * mm});
            skPoint(sketch, "E712", {"position": v(-2.31, -11.77) * mm});
            skPoint(sketch, "E713", {"position": v(-2.5, -12.76) * mm});
            skPoint(sketch, "E714", {"position": v(-2.7, -13.74) * mm});
            skPoint(sketch, "E715", {"position": v(-2.9, -14.72) * mm});
            skPoint(sketch, "E716", {"position": v(-3.08, -15.7) * mm});
            skPoint(sketch, "E717", {"position": v(-3.28, -16.68) * mm});
            skPoint(sketch, "E718", {"position": v(-3.47, -17.66) * mm});
            skPoint(sketch, "E719", {"position": v(-3.66, -18.64) * mm});
            skPoint(sketch, "E720", {"position": v(-3.86, -19.62) * mm});
            skPoint(sketch, "E721", {"position": v(-4.05, -20.6) * mm});
            skPoint(sketch, "E722", {"position": v(-4.24, -21.59) * mm});
            skPoint(sketch, "E723", {"position": v(-4.43, -22.57) * mm});
            skPoint(sketch, "E724", {"position": v(-12.73, -19.15) * mm});
            skPoint(sketch, "E725", {"position": v(-12.18, -18.32) * mm});
            skPoint(sketch, "E726", {"position": v(-11.63, -17.49) * mm});
            skPoint(sketch, "E727", {"position": v(-11.07, -16.66) * mm});
            skPoint(sketch, "E728", {"position": v(-10.52, -15.82) * mm});
            skPoint(sketch, "E729", {"position": v(-9.96, -15) * mm});
            skPoint(sketch, "E730", {"position": v(-9.41, -14.16) * mm});
            skPoint(sketch, "E731", {"position": v(-8.86, -13.32) * mm});
            skPoint(sketch, "E732", {"position": v(-8.3, -12.5) * mm});
            skPoint(sketch, "E733", {"position": v(-7.75, -11.66) * mm});
            skPoint(sketch, "E734", {"position": v(-7.2, -10.83) * mm});
            skPoint(sketch, "E735", {"position": v(-6.64, -10) * mm});
            skPoint(sketch, "E736", {"position": v(-6.09, -9.16) * mm});
            skPoint(sketch, "E737", {"position": v(-5.54, -8.33) * mm});
            skPoint(sketch, "E738", {"position": v(-4.98, -7.5) * mm});
            skPoint(sketch, "E739", {"position": v(-2.77, -4.16) * mm});
            skPoint(sketch, "E740", {"position": v(-2.21, -3.33) * mm});
            skPoint(sketch, "E741", {"position": v(-1.66, -2.5) * mm});
            skPoint(sketch, "E742", {"position": v(-7.47, -5.02) * mm});
            skPoint(sketch, "E743", {"position": v(-8.3, -5.58) * mm});
            skPoint(sketch, "E744", {"position": v(-9.13, -6.13) * mm});
            skPoint(sketch, "E745", {"position": v(-9.96, -6.7) * mm});
            skPoint(sketch, "E746", {"position": v(-10.8, -7.25) * mm});
            skPoint(sketch, "E747", {"position": v(-11.62, -7.8) * mm});
            skPoint(sketch, "E748", {"position": v(-12.45, -8.36) * mm});
            skPoint(sketch, "E749", {"position": v(-13.28, -8.92) * mm});
            skPoint(sketch, "E750", {"position": v(-14.11, -9.48) * mm});
            skPoint(sketch, "E751", {"position": v(-14.94, -10.04) * mm});
            skPoint(sketch, "E752", {"position": v(-15.77, -10.6) * mm});
            skPoint(sketch, "E753", {"position": v(-16.6, -11.15) * mm});
            skPoint(sketch, "E754", {"position": v(-17.43, -11.7) * mm});
            skPoint(sketch, "E755", {"position": v(-18.26, -12.27) * mm});
            skPoint(sketch, "E756", {"position": v(-19.1, -12.82) * mm});
            skPoint(sketch, "E757", {"position": v(-8.82, -1.78) * mm});
            skPoint(sketch, "E758", {"position": v(-9.8, -1.97) * mm});
            skPoint(sketch, "E759", {"position": v(-10.78, -2.17) * mm});
            skPoint(sketch, "E760", {"position": v(-11.76, -2.37) * mm});
            skPoint(sketch, "E761", {"position": v(-12.74, -2.57) * mm});
            skPoint(sketch, "E762", {"position": v(-13.72, -2.76) * mm});
            skPoint(sketch, "E763", {"position": v(-14.7, -2.96) * mm});
            skPoint(sketch, "E764", {"position": v(-15.69, -3.16) * mm});
            skPoint(sketch, "E765", {"position": v(-17.65, -3.55) * mm});
            skPoint(sketch, "E766", {"position": v(-16.67, -3.36) * mm});
            skPoint(sketch, "E767", {"position": v(-18.63, -3.75) * mm});
            skPoint(sketch, "E768", {"position": v(-19.6, -3.95) * mm});
            skPoint(sketch, "E769", {"position": v(-20.59, -4.15) * mm});
            skPoint(sketch, "E770", {"position": v(-21.57, -4.34) * mm});
            skPoint(sketch, "E771", {"position": v(-22.55, -4.54) * mm});
            skPoint(sketch, "E772", {"position": v(-8.83, 1.73) * mm});
            skPoint(sketch, "E773", {"position": v(-7.5, 4.98) * mm});
            skPoint(sketch, "E774", {"position": v(-9.81, 1.93) * mm});
            skPoint(sketch, "E775", {"position": v(-8.33, 5.54) * mm});
            skPoint(sketch, "E776", {"position": v(-10.8, 2.12) * mm});
            skPoint(sketch, "E777", {"position": v(-11.77, 2.31) * mm});
            skPoint(sketch, "E778", {"position": v(-12.76, 2.5) * mm});
            skPoint(sketch, "E779", {"position": v(-13.74, 2.7) * mm});
            skPoint(sketch, "E780", {"position": v(-14.72, 2.9) * mm});
            skPoint(sketch, "E781", {"position": v(-15.7, 3.08) * mm});
            skPoint(sketch, "E782", {"position": v(-16.68, 3.28) * mm});
            skPoint(sketch, "E783", {"position": v(-17.66, 3.47) * mm});
            skPoint(sketch, "E784", {"position": v(-18.64, 3.66) * mm});
            skPoint(sketch, "E785", {"position": v(-19.62, 3.86) * mm});
            skPoint(sketch, "E786", {"position": v(-20.6, 4.05) * mm});
            skPoint(sketch, "E787", {"position": v(-21.59, 4.24) * mm});
            skPoint(sketch, "E788", {"position": v(-22.57, 4.43) * mm});
            skPoint(sketch, "E789", {"position": v(-9.16, 6.09) * mm});
            skPoint(sketch, "E790", {"position": v(-10, 6.64) * mm});
            skPoint(sketch, "E791", {"position": v(-10.83, 7.2) * mm});
            skPoint(sketch, "E792", {"position": v(-11.66, 7.75) * mm});
            skPoint(sketch, "E793", {"position": v(-12.5, 8.3) * mm});
            skPoint(sketch, "E794", {"position": v(-13.32, 8.86) * mm});
            skPoint(sketch, "E795", {"position": v(-14.16, 9.41) * mm});
            skPoint(sketch, "E796", {"position": v(-15, 9.96) * mm});
            skPoint(sketch, "E797", {"position": v(-15.82, 10.52) * mm});
            skPoint(sketch, "E798", {"position": v(-16.66, 11.07) * mm});
            skPoint(sketch, "E799", {"position": v(-17.49, 11.63) * mm});
            skPoint(sketch, "E800", {"position": v(-18.32, 12.18) * mm});
            skPoint(sketch, "E801", {"position": v(-19.15, 12.73) * mm});
            skPoint(sketch, "E802", {"position": v(-5.02, 7.47) * mm});
            skPoint(sketch, "E803", {"position": v(-5.58, 8.3) * mm});
            skPoint(sketch, "E804", {"position": v(-6.13, 9.13) * mm});
            skPoint(sketch, "E805", {"position": v(-6.7, 9.96) * mm});
            skPoint(sketch, "E806", {"position": v(-7.25, 10.8) * mm});
            skPoint(sketch, "E807", {"position": v(-7.8, 11.62) * mm});
            skPoint(sketch, "E808", {"position": v(-8.36, 12.45) * mm});
            skPoint(sketch, "E809", {"position": v(-8.92, 13.28) * mm});
            skPoint(sketch, "E810", {"position": v(-9.48, 14.11) * mm});
            skPoint(sketch, "E811", {"position": v(-10.04, 14.94) * mm});
            skPoint(sketch, "E812", {"position": v(-10.6, 15.77) * mm});
            skPoint(sketch, "E813", {"position": v(-11.15, 16.6) * mm});
            skPoint(sketch, "E814", {"position": v(-11.7, 17.43) * mm});
            skPoint(sketch, "E815", {"position": v(-12.27, 18.26) * mm});
            skPoint(sketch, "E816", {"position": v(-12.82, 19.1) * mm});
            skPoint(sketch, "E817", {"position": v(1.42, -1.41) * mm});
            skPoint(sketch, "E818", {"position": v(-7.7, 18.46) * mm});
            skPoint(sketch, "E819", {"position": v(-8.85, 21.23) * mm});
            skPoint(sketch, "E820", {"position": v(-2.5, 1.66) * mm});
            skSolve(sketch);
        }
        {
            var Q0;
            Q0=makeQuery(id+"F1.opRevolve","SWEPT_EDGE",EDGE,{"disambiguationData":[OSD([sQuery(id+"F0.wireOp",EDGE,"E17"),sQuery(id+"F0.wireOp",EDGE,"E18")])]});
            var Q1;
            Q1=makeQuery(id+"F1.opRevolve","SWEPT_EDGE",EDGE,{"disambiguationData":[OSD([sQuery(id+"F0.wireOp",EDGE,"E8"),sQuery(id+"F0.wireOp",EDGE,"E14"),sQuery(id+"F0.wireOp",EDGE,"E16")])]});
            fillet(context, id + "F4", {"entities" : qUnion([Q0, Q1]), "radius" : 1 * mm, "tangentPropagation" : true, "allowEdgeOverflow" : false});
        }
        {
            var Q0;
            Q0=sQuery(id+"F3.wireOp",VERTEX,"E19.center");
            var Q1;
            Q1=makeQuery(id+"F1.opRevolve","SWEPT_BODY",BODY,{"disambiguationData":[OSD([sQuery(id+"F0.wireOp",EDGE,"E3"),sQuery(id+"F0.wireOp",EDGE,"E4"),sQuery(id+"F0.wireOp",EDGE,"E5"),sQuery(id+"F0.wireOp",EDGE,"E6"),sQuery(id+"F0.wireOp",EDGE,"E8"),sQuery(id+"F0.wireOp",EDGE,"E10"),sQuery(id+"F0.wireOp",EDGE,"E12"),sQuery(id+"F0.wireOp",EDGE,"E15"),sQuery(id+"F0.wireOp",EDGE,"E16"),sQuery(id+"F0.wireOp",EDGE,"E17"),sQuery(id+"F0.wireOp",EDGE,"E18")])]});
            hole(context, id + "F5", {"style" : HoleStyle.SIMPLE, "endStyle" : HoleEndStyle.BLIND, "holeDiameter" : 1.2 * mm, "holeDepth" : 1 * mm, "tappedDepth" : 12 * mm, "tapClearance" : 3, "locations" : qUnion([Q0]), "scope" : qUnion([Q1])});
        }
        {
            var Q0;
            Q0=sQuery(id+"F3.wireOp",VERTEX,"E622");
            var Q1;
            Q1=sQuery(id+"F3.wireOp",VERTEX,"E610");
            var Q2;
            Q2=sQuery(id+"F3.wireOp",VERTEX,"E613");
            var Q3;
            Q3=sQuery(id+"F3.wireOp",VERTEX,"E628");
            var Q4;
            Q4=sQuery(id+"F3.wireOp",VERTEX,"E304");
            var Q5;
            Q5=sQuery(id+"F3.wireOp",VERTEX,"E191");
            var Q6;
            Q6=sQuery(id+"F3.wireOp",VERTEX,"E477");
            var Q7;
            Q7=sQuery(id+"F3.wireOp",VERTEX,"E123");
            var Q8;
            Q8=makeQuery(id+"F1.opRevolve","SWEPT_BODY",BODY,{"disambiguationData":[OSD([sQuery(id+"F0.wireOp",EDGE,"E3"),sQuery(id+"F0.wireOp",EDGE,"E4"),sQuery(id+"F0.wireOp",EDGE,"E5"),sQuery(id+"F0.wireOp",EDGE,"E6"),sQuery(id+"F0.wireOp",EDGE,"E8"),sQuery(id+"F0.wireOp",EDGE,"E10"),sQuery(id+"F0.wireOp",EDGE,"E12"),sQuery(id+"F0.wireOp",EDGE,"E15"),sQuery(id+"F0.wireOp",EDGE,"E16"),sQuery(id+"F0.wireOp",EDGE,"E17"),sQuery(id+"F0.wireOp",EDGE,"E18")])]});
            hole(context, id + "F6", {"style" : HoleStyle.SIMPLE, "endStyle" : HoleEndStyle.BLIND, "holeDiameter" : 1.2 * mm, "holeDepth" : 1 * mm, "tappedDepth" : 12 * mm, "tapClearance" : 3, "locations" : qUnion([Q0, Q1, Q2, Q3, Q4, Q5, Q6, Q7]), "scope" : qUnion([Q8])});
        }
        {
            var Q0;
            Q0=sQuery(id+"F3.wireOp",VERTEX,"E642");
            var Q1;
            Q1=sQuery(id+"F3.wireOp",VERTEX,"E640");
            var Q2;
            Q2=sQuery(id+"F3.wireOp",VERTEX,"E739");
            var Q3;
            Q3=sQuery(id+"F3.wireOp",VERTEX,"E654");
            var Q4;
            Q4=sQuery(id+"F3.wireOp",VERTEX,"E656");
            var Q5;
            Q5=sQuery(id+"F3.wireOp",VERTEX,"E660");
            var Q6;
            Q6=sQuery(id+"F3.wireOp",VERTEX,"E547");
            var Q7;
            Q7=sQuery(id+"F3.wireOp",VERTEX,"E524");
            var Q8;
            Q8=sQuery(id+"F3.wireOp",VERTEX,"E501");
            var Q9;
            Q9=sQuery(id+"F3.wireOp",VERTEX,"E495");
            var Q10;
            Q10=sQuery(id+"F3.wireOp",VERTEX,"E475");
            var Q11;
            Q11=sQuery(id+"F3.wireOp",VERTEX,"E450");
            var Q12;
            Q12=sQuery(id+"F3.wireOp",VERTEX,"E428");
            var Q13;
            Q13=sQuery(id+"F3.wireOp",VERTEX,"E645");
            var Q14;
            Q14=sQuery(id+"F3.wireOp",VERTEX,"E644");
            var Q15;
            Q15=sQuery(id+"F3.wireOp",VERTEX,"E643");
            var Q16;
            Q16=makeQuery(id+"F1.opRevolve","SWEPT_BODY",BODY,{"disambiguationData":[OSD([sQuery(id+"F0.wireOp",EDGE,"E3"),sQuery(id+"F0.wireOp",EDGE,"E4"),sQuery(id+"F0.wireOp",EDGE,"E5"),sQuery(id+"F0.wireOp",EDGE,"E6"),sQuery(id+"F0.wireOp",EDGE,"E8"),sQuery(id+"F0.wireOp",EDGE,"E10"),sQuery(id+"F0.wireOp",EDGE,"E12"),sQuery(id+"F0.wireOp",EDGE,"E15"),sQuery(id+"F0.wireOp",EDGE,"E16"),sQuery(id+"F0.wireOp",EDGE,"E17"),sQuery(id+"F0.wireOp",EDGE,"E18")])]});
            hole(context, id + "F7", {"style" : HoleStyle.SIMPLE, "endStyle" : HoleEndStyle.BLIND, "holeDiameter" : 1.2 * mm, "holeDepth" : 1 * mm, "tappedDepth" : 12 * mm, "tapClearance" : 3, "locations" : qUnion([Q0, Q1, Q2, Q3, Q4, Q5, Q6, Q7, Q8, Q9, Q10, Q11, Q12, Q13, Q14, Q15]), "scope" : qUnion([Q16])});
        }
        {
            var Q0;
            Q0=sQuery(id+"F3.wireOp",VERTEX,"E308");
            var Q1;
            Q1=sQuery(id+"F3.wireOp",VERTEX,"E332");
            var Q2;
            Q2=sQuery(id+"F3.wireOp",VERTEX,"E350");
            var Q3;
            Q3=sQuery(id+"F3.wireOp",VERTEX,"E383");
            var Q4;
            Q4=sQuery(id+"F3.wireOp",VERTEX,"E390");
            var Q5;
            Q5=sQuery(id+"F3.wireOp",VERTEX,"E258");
            var Q6;
            Q6=sQuery(id+"F3.wireOp",VERTEX,"E68");
            var Q7;
            Q7=sQuery(id+"F3.wireOp",VERTEX,"E265");
            var Q8;
            Q8=sQuery(id+"F3.wireOp",VERTEX,"E221");
            var Q9;
            Q9=sQuery(id+"F3.wireOp",VERTEX,"E200");
            var Q10;
            Q10=sQuery(id+"F3.wireOp",VERTEX,"E185");
            var Q11;
            Q11=sQuery(id+"F3.wireOp",VERTEX,"E150");
            var Q12;
            Q12=sQuery(id+"F3.wireOp",VERTEX,"E127");
            var Q13;
            Q13=sQuery(id+"F3.wireOp",VERTEX,"E104");
            var Q14;
            Q14=sQuery(id+"F3.wireOp",VERTEX,"E47");
            var Q15;
            Q15=sQuery(id+"F3.wireOp",VERTEX,"E285");
            var Q16;
            Q16=makeQuery(id+"F1.opRevolve","SWEPT_BODY",BODY,{"disambiguationData":[OSD([sQuery(id+"F0.wireOp",EDGE,"E3"),sQuery(id+"F0.wireOp",EDGE,"E4"),sQuery(id+"F0.wireOp",EDGE,"E5"),sQuery(id+"F0.wireOp",EDGE,"E6"),sQuery(id+"F0.wireOp",EDGE,"E8"),sQuery(id+"F0.wireOp",EDGE,"E10"),sQuery(id+"F0.wireOp",EDGE,"E12"),sQuery(id+"F0.wireOp",EDGE,"E15"),sQuery(id+"F0.wireOp",EDGE,"E16"),sQuery(id+"F0.wireOp",EDGE,"E17"),sQuery(id+"F0.wireOp",EDGE,"E18")])]});
            hole(context, id + "F8", {"style" : HoleStyle.SIMPLE, "endStyle" : HoleEndStyle.BLIND, "holeDiameter" : 1.2 * mm, "holeDepth" : 1 * mm, "tappedDepth" : 12 * mm, "tapClearance" : 3, "locations" : qUnion([Q0, Q1, Q2, Q3, Q4, Q5, Q6, Q7, Q8, Q9, Q10, Q11, Q12, Q13, Q14, Q15]), "scope" : qUnion([Q16])});
        }
        {
            var Q0;
            Q0=sQuery(id+"F3.wireOp",VERTEX,"E446");
            var Q1;
            Q1=sQuery(id+"F3.wireOp",VERTEX,"E471");
            var Q2;
            Q2=sQuery(id+"F3.wireOp",VERTEX,"E491");
            var Q3;
            Q3=sQuery(id+"F3.wireOp",VERTEX,"E505");
            var Q4;
            Q4=sQuery(id+"F3.wireOp",VERTEX,"E528");
            var Q5;
            Q5=sQuery(id+"F3.wireOp",VERTEX,"E551");
            var Q6;
            Q6=sQuery(id+"F3.wireOp",VERTEX,"E679");
            var Q7;
            Q7=sQuery(id+"F3.wireOp",VERTEX,"E708");
            var Q8;
            Q8=sQuery(id+"F3.wireOp",VERTEX,"E709");
            var Q9;
            Q9=sQuery(id+"F3.wireOp",VERTEX,"E738");
            var Q10;
            Q10=sQuery(id+"F3.wireOp",VERTEX,"E742");
            var Q11;
            Q11=sQuery(id+"F3.wireOp",VERTEX,"E757");
            var Q12;
            Q12=sQuery(id+"F3.wireOp",VERTEX,"E772");
            var Q13;
            Q13=sQuery(id+"F3.wireOp",VERTEX,"E773");
            var Q14;
            Q14=sQuery(id+"F3.wireOp",VERTEX,"E802");
            var Q15;
            Q15=sQuery(id+"F3.wireOp",VERTEX,"E424");
            var Q16;
            Q16=makeQuery(id+"F1.opRevolve","SWEPT_BODY",BODY,{"disambiguationData":[OSD([sQuery(id+"F0.wireOp",EDGE,"E3"),sQuery(id+"F0.wireOp",EDGE,"E4"),sQuery(id+"F0.wireOp",EDGE,"E5"),sQuery(id+"F0.wireOp",EDGE,"E6"),sQuery(id+"F0.wireOp",EDGE,"E8"),sQuery(id+"F0.wireOp",EDGE,"E10"),sQuery(id+"F0.wireOp",EDGE,"E12"),sQuery(id+"F0.wireOp",EDGE,"E15"),sQuery(id+"F0.wireOp",EDGE,"E16"),sQuery(id+"F0.wireOp",EDGE,"E17"),sQuery(id+"F0.wireOp",EDGE,"E18")])]});
            hole(context, id + "F9", {"style" : HoleStyle.SIMPLE, "endStyle" : HoleEndStyle.BLIND, "holeDiameter" : 1.2 * mm, "holeDepth" : 1 * mm, "tappedDepth" : 12 * mm, "tapClearance" : 3, "locations" : qUnion([Q0, Q1, Q2, Q3, Q4, Q5, Q6, Q7, Q8, Q9, Q10, Q11, Q12, Q13, Q14, Q15]), "scope" : qUnion([Q16])});
        }
        {
            var Q0;
            Q0=sQuery(id+"F3.wireOp",VERTEX,"E131");
            var Q1;
            Q1=sQuery(id+"F3.wireOp",VERTEX,"E154");
            var Q2;
            Q2=sQuery(id+"F3.wireOp",VERTEX,"E181");
            var Q3;
            Q3=sQuery(id+"F3.wireOp",VERTEX,"E204");
            var Q4;
            Q4=sQuery(id+"F3.wireOp",VERTEX,"E225");
            var Q5;
            Q5=sQuery(id+"F3.wireOp",VERTEX,"E269");
            var Q6;
            Q6=sQuery(id+"F3.wireOp",VERTEX,"E72");
            var Q7;
            Q7=sQuery(id+"F3.wireOp",VERTEX,"E254");
            var Q8;
            Q8=sQuery(id+"F3.wireOp",VERTEX,"E394");
            var Q9;
            Q9=sQuery(id+"F3.wireOp",VERTEX,"E379");
            var Q10;
            Q10=sQuery(id+"F3.wireOp",VERTEX,"E365");
            var Q11;
            Q11=sQuery(id+"F3.wireOp",VERTEX,"E336");
            var Q12;
            Q12=sQuery(id+"F3.wireOp",VERTEX,"E312");
            var Q13;
            Q13=sQuery(id+"F3.wireOp",VERTEX,"E289");
            var Q14;
            Q14=sQuery(id+"F3.wireOp",VERTEX,"E51");
            var Q15;
            Q15=sQuery(id+"F3.wireOp",VERTEX,"E108");
            var Q16;
            Q16=makeQuery(id+"F1.opRevolve","SWEPT_BODY",BODY,{"disambiguationData":[OSD([sQuery(id+"F0.wireOp",EDGE,"E3"),sQuery(id+"F0.wireOp",EDGE,"E4"),sQuery(id+"F0.wireOp",EDGE,"E5"),sQuery(id+"F0.wireOp",EDGE,"E6"),sQuery(id+"F0.wireOp",EDGE,"E8"),sQuery(id+"F0.wireOp",EDGE,"E10"),sQuery(id+"F0.wireOp",EDGE,"E12"),sQuery(id+"F0.wireOp",EDGE,"E15"),sQuery(id+"F0.wireOp",EDGE,"E16"),sQuery(id+"F0.wireOp",EDGE,"E17"),sQuery(id+"F0.wireOp",EDGE,"E18")])]});
            hole(context, id + "F10", {"style" : HoleStyle.SIMPLE, "endStyle" : HoleEndStyle.BLIND, "holeDiameter" : 1.2 * mm, "holeDepth" : 1 * mm, "tappedDepth" : 12 * mm, "tapClearance" : 3, "locations" : qUnion([Q0, Q1, Q2, Q3, Q4, Q5, Q6, Q7, Q8, Q9, Q10, Q11, Q12, Q13, Q14, Q15]), "scope" : qUnion([Q16])});
        }
        {
            var Q0;
            Q0=sQuery(id+"F3.wireOp",VERTEX,"E806");
            var Q1;
            Q1=sQuery(id+"F3.wireOp",VERTEX,"E420");
            var Q2;
            Q2=sQuery(id+"F3.wireOp",VERTEX,"E442");
            var Q3;
            Q3=sQuery(id+"F3.wireOp",VERTEX,"E467");
            var Q4;
            Q4=sQuery(id+"F3.wireOp",VERTEX,"E487");
            var Q5;
            Q5=sQuery(id+"F3.wireOp",VERTEX,"E509");
            var Q6;
            Q6=sQuery(id+"F3.wireOp",VERTEX,"E532");
            var Q7;
            Q7=sQuery(id+"F3.wireOp",VERTEX,"E581");
            var Q8;
            Q8=sQuery(id+"F3.wireOp",VERTEX,"E683");
            var Q9;
            Q9=sQuery(id+"F3.wireOp",VERTEX,"E704");
            var Q10;
            Q10=sQuery(id+"F3.wireOp",VERTEX,"E713");
            var Q11;
            Q11=sQuery(id+"F3.wireOp",VERTEX,"E734");
            var Q12;
            Q12=sQuery(id+"F3.wireOp",VERTEX,"E746");
            var Q13;
            Q13=sQuery(id+"F3.wireOp",VERTEX,"E761");
            var Q14;
            Q14=sQuery(id+"F3.wireOp",VERTEX,"E778");
            var Q15;
            Q15=sQuery(id+"F3.wireOp",VERTEX,"E791");
            var Q16;
            Q16=makeQuery(id+"F1.opRevolve","SWEPT_BODY",BODY,{"disambiguationData":[OSD([sQuery(id+"F0.wireOp",EDGE,"E3"),sQuery(id+"F0.wireOp",EDGE,"E4"),sQuery(id+"F0.wireOp",EDGE,"E5"),sQuery(id+"F0.wireOp",EDGE,"E6"),sQuery(id+"F0.wireOp",EDGE,"E8"),sQuery(id+"F0.wireOp",EDGE,"E10"),sQuery(id+"F0.wireOp",EDGE,"E12"),sQuery(id+"F0.wireOp",EDGE,"E15"),sQuery(id+"F0.wireOp",EDGE,"E16"),sQuery(id+"F0.wireOp",EDGE,"E17"),sQuery(id+"F0.wireOp",EDGE,"E18")])]});
            hole(context, id + "F11", {"style" : HoleStyle.SIMPLE, "endStyle" : HoleEndStyle.BLIND, "holeDiameter" : 1.2 * mm, "holeDepth" : 1 * mm, "tappedDepth" : 12 * mm, "tapClearance" : 3, "locations" : qUnion([Q0, Q1, Q2, Q3, Q4, Q5, Q6, Q7, Q8, Q9, Q10, Q11, Q12, Q13, Q14, Q15]), "scope" : qUnion([Q16])});
        }
        {
            var Q0;
            Q0=sQuery(id+"F3.wireOp",VERTEX,"E292");
            var Q1;
            Q1=sQuery(id+"F3.wireOp",VERTEX,"E315");
            var Q2;
            Q2=sQuery(id+"F3.wireOp",VERTEX,"E339");
            var Q3;
            Q3=sQuery(id+"F3.wireOp",VERTEX,"E362");
            var Q4;
            Q4=sQuery(id+"F3.wireOp",VERTEX,"E376");
            var Q5;
            Q5=sQuery(id+"F3.wireOp",VERTEX,"E397");
            var Q6;
            Q6=sQuery(id+"F3.wireOp",VERTEX,"E251");
            var Q7;
            Q7=sQuery(id+"F3.wireOp",VERTEX,"E75");
            var Q8;
            Q8=sQuery(id+"F3.wireOp",VERTEX,"E272");
            var Q9;
            Q9=sQuery(id+"F3.wireOp",VERTEX,"E228");
            var Q10;
            Q10=sQuery(id+"F3.wireOp",VERTEX,"E207");
            var Q11;
            Q11=sQuery(id+"F3.wireOp",VERTEX,"E178");
            var Q12;
            Q12=sQuery(id+"F3.wireOp",VERTEX,"E157");
            var Q13;
            Q13=sQuery(id+"F3.wireOp",VERTEX,"E134");
            var Q14;
            Q14=sQuery(id+"F3.wireOp",VERTEX,"E111");
            var Q15;
            Q15=sQuery(id+"F3.wireOp",VERTEX,"E54");
            var Q16;
            Q16=makeQuery(id+"F1.opRevolve","SWEPT_BODY",BODY,{"disambiguationData":[OSD([sQuery(id+"F0.wireOp",EDGE,"E3"),sQuery(id+"F0.wireOp",EDGE,"E4"),sQuery(id+"F0.wireOp",EDGE,"E5"),sQuery(id+"F0.wireOp",EDGE,"E6"),sQuery(id+"F0.wireOp",EDGE,"E8"),sQuery(id+"F0.wireOp",EDGE,"E10"),sQuery(id+"F0.wireOp",EDGE,"E12"),sQuery(id+"F0.wireOp",EDGE,"E15"),sQuery(id+"F0.wireOp",EDGE,"E16"),sQuery(id+"F0.wireOp",EDGE,"E17"),sQuery(id+"F0.wireOp",EDGE,"E18")])]});
            hole(context, id + "F12", {"style" : HoleStyle.SIMPLE, "endStyle" : HoleEndStyle.BLIND, "holeDiameter" : 1.2 * mm, "holeDepth" : 1 * mm, "tappedDepth" : 12 * mm, "tapClearance" : 3, "locations" : qUnion([Q0, Q1, Q2, Q3, Q4, Q5, Q6, Q7, Q8, Q9, Q10, Q11, Q12, Q13, Q14, Q15]), "scope" : qUnion([Q16])});
        }
        {
            var Q0;
            Q0=sQuery(id+"F3.wireOp",VERTEX,"E794");
            var Q1;
            Q1=sQuery(id+"F3.wireOp",VERTEX,"E809");
            var Q2;
            Q2=sQuery(id+"F3.wireOp",VERTEX,"E417");
            var Q3;
            Q3=sQuery(id+"F3.wireOp",VERTEX,"E439");
            var Q4;
            Q4=sQuery(id+"F3.wireOp",VERTEX,"E464");
            var Q5;
            Q5=sQuery(id+"F3.wireOp",VERTEX,"E484");
            var Q6;
            Q6=sQuery(id+"F3.wireOp",VERTEX,"E512");
            var Q7;
            Q7=sQuery(id+"F3.wireOp",VERTEX,"E535");
            var Q8;
            Q8=sQuery(id+"F3.wireOp",VERTEX,"E578");
            var Q9;
            Q9=sQuery(id+"F3.wireOp",VERTEX,"E686");
            var Q10;
            Q10=sQuery(id+"F3.wireOp",VERTEX,"E701");
            var Q11;
            Q11=sQuery(id+"F3.wireOp",VERTEX,"E716");
            var Q12;
            Q12=sQuery(id+"F3.wireOp",VERTEX,"E731");
            var Q13;
            Q13=sQuery(id+"F3.wireOp",VERTEX,"E749");
            var Q14;
            Q14=sQuery(id+"F3.wireOp",VERTEX,"E764");
            var Q15;
            Q15=sQuery(id+"F3.wireOp",VERTEX,"E781");
            var Q16;
            Q16=makeQuery(id+"F1.opRevolve","SWEPT_BODY",BODY,{"disambiguationData":[OSD([sQuery(id+"F0.wireOp",EDGE,"E3"),sQuery(id+"F0.wireOp",EDGE,"E4"),sQuery(id+"F0.wireOp",EDGE,"E5"),sQuery(id+"F0.wireOp",EDGE,"E6"),sQuery(id+"F0.wireOp",EDGE,"E8"),sQuery(id+"F0.wireOp",EDGE,"E10"),sQuery(id+"F0.wireOp",EDGE,"E12"),sQuery(id+"F0.wireOp",EDGE,"E15"),sQuery(id+"F0.wireOp",EDGE,"E16"),sQuery(id+"F0.wireOp",EDGE,"E17"),sQuery(id+"F0.wireOp",EDGE,"E18")])]});
            hole(context, id + "F13", {"style" : HoleStyle.SIMPLE, "endStyle" : HoleEndStyle.BLIND, "holeDiameter" : 1.2 * mm, "holeDepth" : 1 * mm, "tappedDepth" : 12 * mm, "tapClearance" : 3, "locations" : qUnion([Q0, Q1, Q2, Q3, Q4, Q5, Q6, Q7, Q8, Q9, Q10, Q11, Q12, Q13, Q14, Q15]), "scope" : qUnion([Q16])});
        }
        {
            var Q0;
            Q0=sQuery(id+"F3.wireOp",VERTEX,"E318");
            var Q1;
            Q1=sQuery(id+"F3.wireOp",VERTEX,"E342");
            var Q2;
            Q2=sQuery(id+"F3.wireOp",VERTEX,"E359");
            var Q3;
            Q3=sQuery(id+"F3.wireOp",VERTEX,"E373");
            var Q4;
            Q4=sQuery(id+"F3.wireOp",VERTEX,"E400");
            var Q5;
            Q5=sQuery(id+"F3.wireOp",VERTEX,"E248");
            var Q6;
            Q6=sQuery(id+"F3.wireOp",VERTEX,"E78");
            var Q7;
            Q7=sQuery(id+"F3.wireOp",VERTEX,"E275");
            var Q8;
            Q8=sQuery(id+"F3.wireOp",VERTEX,"E231");
            var Q9;
            Q9=sQuery(id+"F3.wireOp",VERTEX,"E210");
            var Q10;
            Q10=sQuery(id+"F3.wireOp",VERTEX,"E175");
            var Q11;
            Q11=sQuery(id+"F3.wireOp",VERTEX,"E160");
            var Q12;
            Q12=sQuery(id+"F3.wireOp",VERTEX,"E137");
            var Q13;
            Q13=sQuery(id+"F3.wireOp",VERTEX,"E114");
            var Q14;
            Q14=sQuery(id+"F3.wireOp",VERTEX,"E57");
            var Q15;
            Q15=sQuery(id+"F3.wireOp",VERTEX,"E295");
            var Q16;
            Q16=makeQuery(id+"F1.opRevolve","SWEPT_BODY",BODY,{"disambiguationData":[OSD([sQuery(id+"F0.wireOp",EDGE,"E3"),sQuery(id+"F0.wireOp",EDGE,"E4"),sQuery(id+"F0.wireOp",EDGE,"E5"),sQuery(id+"F0.wireOp",EDGE,"E6"),sQuery(id+"F0.wireOp",EDGE,"E8"),sQuery(id+"F0.wireOp",EDGE,"E10"),sQuery(id+"F0.wireOp",EDGE,"E12"),sQuery(id+"F0.wireOp",EDGE,"E15"),sQuery(id+"F0.wireOp",EDGE,"E16"),sQuery(id+"F0.wireOp",EDGE,"E17"),sQuery(id+"F0.wireOp",EDGE,"E18")])]});
            hole(context, id + "F14", {"style" : HoleStyle.SIMPLE, "endStyle" : HoleEndStyle.BLIND, "holeDiameter" : 1.2 * mm, "holeDepth" : 1 * mm, "tappedDepth" : 12 * mm, "tapClearance" : 3, "locations" : qUnion([Q0, Q1, Q2, Q3, Q4, Q5, Q6, Q7, Q8, Q9, Q10, Q11, Q12, Q13, Q14, Q15]), "scope" : qUnion([Q16])});
        }
        {
            var Q0;
            Q0=sQuery(id+"F3.wireOp",VERTEX,"E767");
            var Q1;
            Q1=sQuery(id+"F3.wireOp",VERTEX,"E784");
            var Q2;
            Q2=sQuery(id+"F3.wireOp",VERTEX,"E797");
            var Q3;
            Q3=sQuery(id+"F3.wireOp",VERTEX,"E812");
            var Q4;
            Q4=sQuery(id+"F3.wireOp",VERTEX,"E414");
            var Q5;
            Q5=sQuery(id+"F3.wireOp",VERTEX,"E436");
            var Q6;
            Q6=sQuery(id+"F3.wireOp",VERTEX,"E461");
            var Q7;
            Q7=sQuery(id+"F3.wireOp",VERTEX,"E481");
            var Q8;
            Q8=sQuery(id+"F3.wireOp",VERTEX,"E515");
            var Q9;
            Q9=sQuery(id+"F3.wireOp",VERTEX,"E538");
            var Q10;
            Q10=sQuery(id+"F3.wireOp",VERTEX,"E575");
            var Q11;
            Q11=sQuery(id+"F3.wireOp",VERTEX,"E689");
            var Q12;
            Q12=sQuery(id+"F3.wireOp",VERTEX,"E698");
            var Q13;
            Q13=sQuery(id+"F3.wireOp",VERTEX,"E719");
            var Q14;
            Q14=sQuery(id+"F3.wireOp",VERTEX,"E728");
            var Q15;
            Q15=sQuery(id+"F3.wireOp",VERTEX,"E752");
            var Q16;
            Q16=makeQuery(id+"F1.opRevolve","SWEPT_BODY",BODY,{"disambiguationData":[OSD([sQuery(id+"F0.wireOp",EDGE,"E3"),sQuery(id+"F0.wireOp",EDGE,"E4"),sQuery(id+"F0.wireOp",EDGE,"E5"),sQuery(id+"F0.wireOp",EDGE,"E6"),sQuery(id+"F0.wireOp",EDGE,"E8"),sQuery(id+"F0.wireOp",EDGE,"E10"),sQuery(id+"F0.wireOp",EDGE,"E12"),sQuery(id+"F0.wireOp",EDGE,"E15"),sQuery(id+"F0.wireOp",EDGE,"E16"),sQuery(id+"F0.wireOp",EDGE,"E17"),sQuery(id+"F0.wireOp",EDGE,"E18")])]});
            hole(context, id + "F15", {"style" : HoleStyle.SIMPLE, "endStyle" : HoleEndStyle.BLIND, "holeDiameter" : 1.2 * mm, "holeDepth" : 1 * mm, "tappedDepth" : 12 * mm, "tapClearance" : 3, "locations" : qUnion([Q0, Q1, Q2, Q3, Q4, Q5, Q6, Q7, Q8, Q9, Q10, Q11, Q12, Q13, Q14, Q15]), "scope" : qUnion([Q16])});
        }
        {
            var Q0;
            Q0=sQuery(id+"F3.wireOp",VERTEX,"E298");
            var Q1;
            Q1=sQuery(id+"F3.wireOp",VERTEX,"E321");
            var Q2;
            Q2=sQuery(id+"F3.wireOp",VERTEX,"E818");
            var Q3;
            Q3=sQuery(id+"F3.wireOp",VERTEX,"E356");
            var Q4;
            Q4=sQuery(id+"F3.wireOp",VERTEX,"E370");
            var Q5;
            Q5=sQuery(id+"F3.wireOp",VERTEX,"E403");
            var Q6;
            Q6=sQuery(id+"F3.wireOp",VERTEX,"E245");
            var Q7;
            Q7=sQuery(id+"F3.wireOp",VERTEX,"E81");
            var Q8;
            Q8=sQuery(id+"F3.wireOp",VERTEX,"E278");
            var Q9;
            Q9=sQuery(id+"F3.wireOp",VERTEX,"E234");
            var Q10;
            Q10=sQuery(id+"F3.wireOp",VERTEX,"E213");
            var Q11;
            Q11=sQuery(id+"F3.wireOp",VERTEX,"E172");
            var Q12;
            Q12=sQuery(id+"F3.wireOp",VERTEX,"E163");
            var Q13;
            Q13=sQuery(id+"F3.wireOp",VERTEX,"E140");
            var Q14;
            Q14=sQuery(id+"F3.wireOp",VERTEX,"E117");
            var Q15;
            Q15=sQuery(id+"F3.wireOp",VERTEX,"E60");
            var Q16;
            Q16=makeQuery(id+"F1.opRevolve","SWEPT_BODY",BODY,{"disambiguationData":[OSD([sQuery(id+"F0.wireOp",EDGE,"E3"),sQuery(id+"F0.wireOp",EDGE,"E4"),sQuery(id+"F0.wireOp",EDGE,"E5"),sQuery(id+"F0.wireOp",EDGE,"E6"),sQuery(id+"F0.wireOp",EDGE,"E8"),sQuery(id+"F0.wireOp",EDGE,"E10"),sQuery(id+"F0.wireOp",EDGE,"E12"),sQuery(id+"F0.wireOp",EDGE,"E15"),sQuery(id+"F0.wireOp",EDGE,"E16"),sQuery(id+"F0.wireOp",EDGE,"E17"),sQuery(id+"F0.wireOp",EDGE,"E18")])]});
            hole(context, id + "F16", {"style" : HoleStyle.SIMPLE, "endStyle" : HoleEndStyle.BLIND, "holeDiameter" : 1.2 * mm, "holeDepth" : 1 * mm, "tappedDepth" : 12 * mm, "tapClearance" : 3, "locations" : qUnion([Q0, Q1, Q2, Q3, Q4, Q5, Q6, Q7, Q8, Q9, Q10, Q11, Q12, Q13, Q14, Q15]), "scope" : qUnion([Q16])});
        }
        {
            var Q0;
            Q0=sQuery(id+"F3.wireOp",VERTEX,"E770");
            var Q1;
            Q1=sQuery(id+"F3.wireOp",VERTEX,"E787");
            var Q2;
            Q2=sQuery(id+"F3.wireOp",VERTEX,"E800");
            var Q3;
            Q3=sQuery(id+"F3.wireOp",VERTEX,"E815");
            var Q4;
            Q4=sQuery(id+"F3.wireOp",VERTEX,"E411");
            var Q5;
            Q5=sQuery(id+"F3.wireOp",VERTEX,"E433");
            var Q6;
            Q6=sQuery(id+"F3.wireOp",VERTEX,"E458");
            var Q7;
            Q7=sQuery(id+"F3.wireOp",VERTEX,"E478");
            var Q8;
            Q8=sQuery(id+"F3.wireOp",VERTEX,"E518");
            var Q9;
            Q9=sQuery(id+"F3.wireOp",VERTEX,"E541");
            var Q10;
            Q10=sQuery(id+"F3.wireOp",VERTEX,"E572");
            var Q11;
            Q11=sQuery(id+"F3.wireOp",VERTEX,"E692");
            var Q12;
            Q12=sQuery(id+"F3.wireOp",VERTEX,"E695");
            var Q13;
            Q13=sQuery(id+"F3.wireOp",VERTEX,"E722");
            var Q14;
            Q14=sQuery(id+"F3.wireOp",VERTEX,"E725");
            var Q15;
            Q15=sQuery(id+"F3.wireOp",VERTEX,"E755");
            var Q16;
            Q16=makeQuery(id+"F1.opRevolve","SWEPT_BODY",BODY,{"disambiguationData":[OSD([sQuery(id+"F0.wireOp",EDGE,"E3"),sQuery(id+"F0.wireOp",EDGE,"E4"),sQuery(id+"F0.wireOp",EDGE,"E5"),sQuery(id+"F0.wireOp",EDGE,"E6"),sQuery(id+"F0.wireOp",EDGE,"E8"),sQuery(id+"F0.wireOp",EDGE,"E10"),sQuery(id+"F0.wireOp",EDGE,"E12"),sQuery(id+"F0.wireOp",EDGE,"E15"),sQuery(id+"F0.wireOp",EDGE,"E16"),sQuery(id+"F0.wireOp",EDGE,"E17"),sQuery(id+"F0.wireOp",EDGE,"E18")])]});
            hole(context, id + "F17", {"style" : HoleStyle.SIMPLE, "endStyle" : HoleEndStyle.BLIND, "holeDiameter" : 1.2 * mm, "holeDepth" : 1 * mm, "tappedDepth" : 12 * mm, "tapClearance" : 3, "locations" : qUnion([Q0, Q1, Q2, Q3, Q4, Q5, Q6, Q7, Q8, Q9, Q10, Q11, Q12, Q13, Q14, Q15]), "scope" : qUnion([Q16])});
        }
        {
            var Q0;
            Q0=sQuery(id+"F3.wireOp",VERTEX,"E326");
            var Q1;
            Q1=sQuery(id+"F3.wireOp",VERTEX,"E327");
            var Q2;
            Q2=sQuery(id+"F3.wireOp",VERTEX,"E328");
            var Q3;
            Q3=sQuery(id+"F3.wireOp",VERTEX,"E329");
            var Q4;
            Q4=sQuery(id+"F3.wireOp",VERTEX,"E240");
            var Q5;
            Q5=sQuery(id+"F3.wireOp",VERTEX,"E85");
            var Q6;
            Q6=sQuery(id+"F3.wireOp",VERTEX,"E239");
            var Q7;
            Q7=sQuery(id+"F3.wireOp",VERTEX,"E238");
            var Q8;
            Q8=sQuery(id+"F3.wireOp",VERTEX,"E217");
            var Q9;
            Q9=sQuery(id+"F3.wireOp",VERTEX,"E168");
            var Q10;
            Q10=sQuery(id+"F3.wireOp",VERTEX,"E167");
            var Q11;
            Q11=sQuery(id+"F3.wireOp",VERTEX,"E144");
            var Q12;
            Q12=sQuery(id+"F3.wireOp",VERTEX,"E121");
            var Q13;
            Q13=sQuery(id+"F3.wireOp",VERTEX,"E64");
            var Q14;
            Q14=sQuery(id+"F3.wireOp",VERTEX,"E302");
            var Q15;
            Q15=sQuery(id+"F3.wireOp",VERTEX,"E325");
            var Q16;
            Q16=makeQuery(id+"F1.opRevolve","SWEPT_BODY",BODY,{"disambiguationData":[OSD([sQuery(id+"F0.wireOp",EDGE,"E3"),sQuery(id+"F0.wireOp",EDGE,"E4"),sQuery(id+"F0.wireOp",EDGE,"E5"),sQuery(id+"F0.wireOp",EDGE,"E6"),sQuery(id+"F0.wireOp",EDGE,"E8"),sQuery(id+"F0.wireOp",EDGE,"E10"),sQuery(id+"F0.wireOp",EDGE,"E12"),sQuery(id+"F0.wireOp",EDGE,"E15"),sQuery(id+"F0.wireOp",EDGE,"E16"),sQuery(id+"F0.wireOp",EDGE,"E17"),sQuery(id+"F0.wireOp",EDGE,"E18")])]});
            hole(context, id + "F18", {"style" : HoleStyle.SIMPLE, "endStyle" : HoleEndStyle.BLIND, "holeDiameter" : 1.2 * mm, "holeDepth" : 1 * mm, "tappedDepth" : 12 * mm, "tapClearance" : 3, "locations" : qUnion([Q0, Q1, Q2, Q3, Q4, Q5, Q6, Q7, Q8, Q9, Q10, Q11, Q12, Q13, Q14, Q15]), "scope" : qUnion([Q16])});
        }
    });
